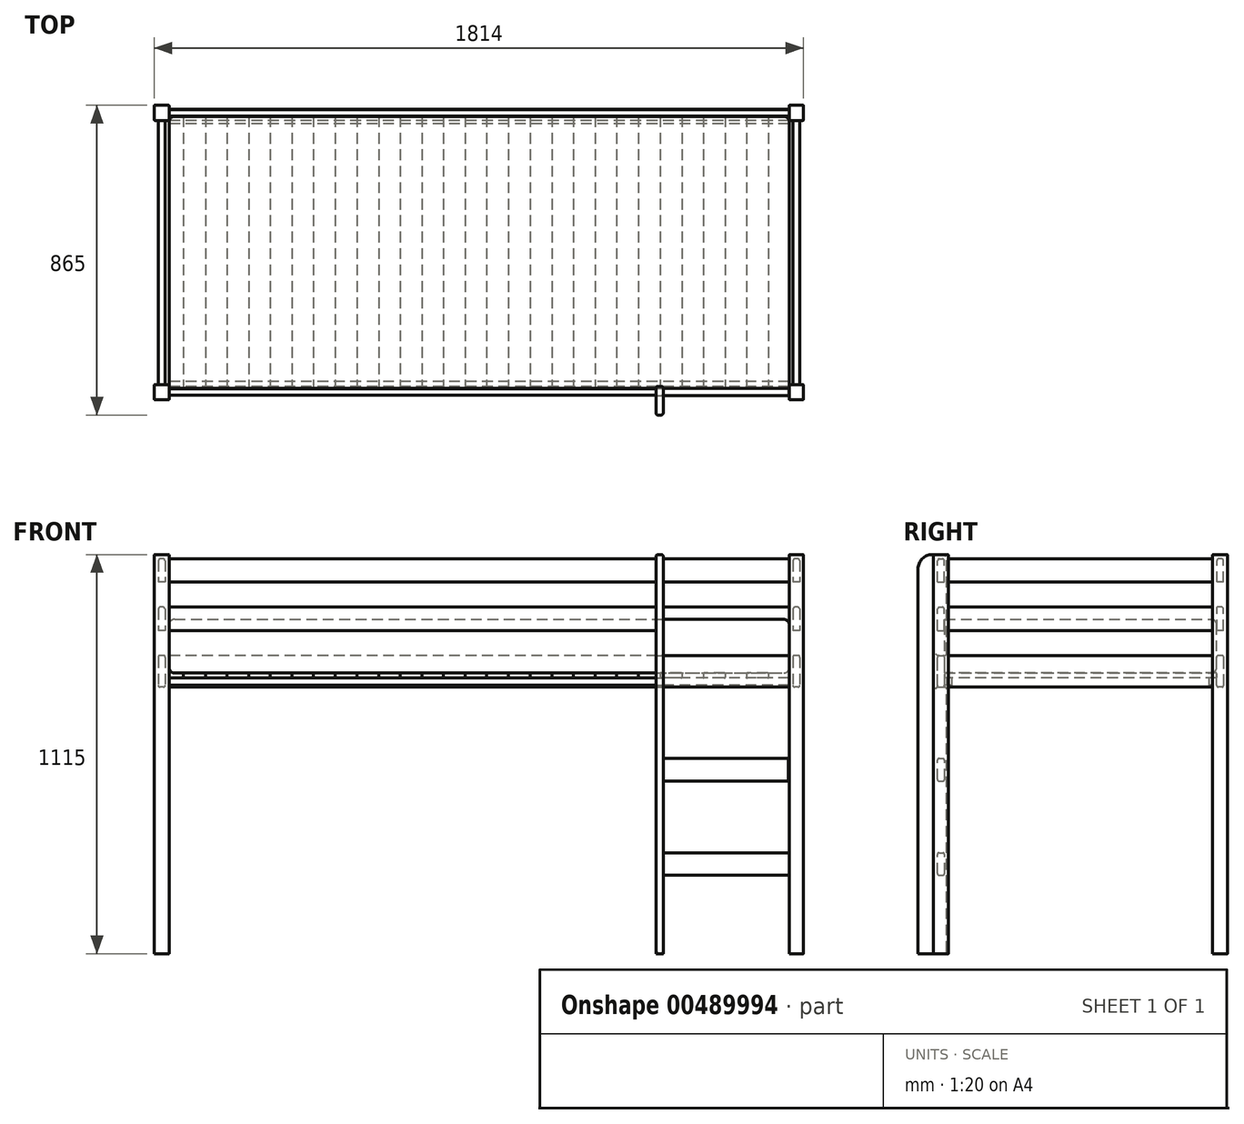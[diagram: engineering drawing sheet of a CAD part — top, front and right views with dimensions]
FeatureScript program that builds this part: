
annotation { "Feature Type Name" : "Feature", "Feature Type Description" : "" }
export const myFeature = defineFeature(function(context is Context, id is Id, definition is map)
    precondition{}
    {
        {
            var Q0;
            Q0=qCreatedBy(makeId("Front.planeOp"),FACE);
            var sketch = newSketch(context, id + "F0", { "sketchPlane" : qUnion([Q0])});
            skLineSegment(sketch, "E0.bottom", {"start": v(0, 0) * mm, "end": v(42, 0) * mm});
            skLineSegment(sketch, "E0.top", {"start": v(0, 1115) * mm, "end": v(42, 1115) * mm});
            skLineSegment(sketch, "E0.left", {"start": v(0, 0) * mm, "end": v(0, 1115) * mm});
            skLineSegment(sketch, "E0.right", {"start": v(42, 0) * mm, "end": v(42, 1115) * mm});
            skLineSegment(sketch, "E1.bottom", {"start": v(42, 745) * mm, "end": v(1774, 745) * mm});
            skLineSegment(sketch, "E1.top", {"start": v(42, 833) * mm, "end": v(1774, 833) * mm});
            skLineSegment(sketch, "E1.left", {"start": v(42, 745) * mm, "end": v(42, 833) * mm});
            skLineSegment(sketch, "E1.right", {"start": v(1774, 745) * mm, "end": v(1774, 833) * mm});
            skLineSegment(sketch, "E2.bottom", {"start": v(1774, 0) * mm, "end": v(1814, 0) * mm});
            skLineSegment(sketch, "E2.top", {"start": v(1774, 1115) * mm, "end": v(1814, 1115) * mm});
            skLineSegment(sketch, "E2.left", {"start": v(1774, 0) * mm, "end": v(1774, 1115) * mm});
            skLineSegment(sketch, "E2.right", {"start": v(1814, 0) * mm, "end": v(1814, 1115) * mm});
            skLineSegment(sketch, "E3.bottom", {"start": v(1402, 0) * mm, "end": v(1422, 0) * mm});
            skLineSegment(sketch, "E3.top", {"start": v(1402, 1115) * mm, "end": v(1422, 1115) * mm});
            skLineSegment(sketch, "E3.left", {"start": v(1402, 0) * mm, "end": v(1402, 1115) * mm});
            skLineSegment(sketch, "E3.right", {"start": v(1422, 0) * mm, "end": v(1422, 1115) * mm});
            skLineSegment(sketch, "E4.bottom", {"start": v(42, 968) * mm, "end": v(1402, 968) * mm});
            skLineSegment(sketch, "E4.top", {"start": v(42, 903) * mm, "end": v(1402, 903) * mm});
            skLineSegment(sketch, "E4.left", {"start": v(42, 968) * mm, "end": v(42, 903) * mm});
            skLineSegment(sketch, "E4.right", {"start": v(1402, 968) * mm, "end": v(1402, 903) * mm});
            skLineSegment(sketch, "E5.bottom", {"start": v(1422, 219) * mm, "end": v(1774, 219) * mm});
            skLineSegment(sketch, "E5.top", {"start": v(1422, 282) * mm, "end": v(1774, 282) * mm});
            skLineSegment(sketch, "E5.left", {"start": v(1422, 219) * mm, "end": v(1422, 282) * mm});
            skLineSegment(sketch, "E5.right", {"start": v(1774, 219) * mm, "end": v(1774, 282) * mm});
            skLineSegment(sketch, "E6.bottom", {"start": v(1422, 482) * mm, "end": v(1772, 482) * mm});
            skLineSegment(sketch, "E6.top", {"start": v(1422, 545) * mm, "end": v(1772, 545) * mm});
            skLineSegment(sketch, "E6.left", {"start": v(1422, 482) * mm, "end": v(1422, 545) * mm});
            skLineSegment(sketch, "E6.right", {"start": v(1772, 482) * mm, "end": v(1772, 545) * mm});
            skLineSegment(sketch, "E7.bottom", {"start": v(42, 1038) * mm, "end": v(1402, 1038) * mm});
            skLineSegment(sketch, "E7.top", {"start": v(42, 1103) * mm, "end": v(1402, 1103) * mm});
            skLineSegment(sketch, "E7.left", {"start": v(42, 1038) * mm, "end": v(42, 1103) * mm});
            skLineSegment(sketch, "E7.right", {"start": v(1402, 1038) * mm, "end": v(1402, 1103) * mm});
            skSolve(sketch);
        }
        {
            var Q0;
            {var subQ3=sQuery(id+"F0.wireOp",EDGE,"E2.bottom");Q0=makeQuery(id+"F0.imprint","IMPRINT",FACE,{"disambiguationData":[TD([[makeQuery(id+"F0.imprint","IMPRINT",EDGE,{"derivedFrom":subQ3}),1.0]])]});}
            var Q1;
            {var subQ1=sQuery(id+"F0.wireOp",EDGE,"E0.bottom");Q1=makeQuery(id+"F0.imprint","IMPRINT",FACE,{"disambiguationData":[TD([[makeQuery(id+"F0.imprint","IMPRINT",EDGE,{"derivedFrom":subQ1}),1.0]])]});}
            extrude(context, id + "F1", {"entities" : qUnion([Q0, Q1]), "depth" : 21 * mm, "hasSecondDirection" : true, "secondDirectionOppositeDirection" : true, "secondDirectionDepth" : 21 * mm});
        }
        {
            var Q0;
            {var subQ0=sQuery(id+"F0.wireOp",EDGE,"E1.left");Q0=makeQuery(id+"F0.imprint","IMPRINT",FACE,{"disambiguationData":[TD([[makeQuery(id+"F0.imprint","IMPRINT",EDGE,{"derivedFrom":subQ0}),-1.0]])]});}
            var Q1;
            {var subQ0=sQuery(id+"F0.wireOp",EDGE,"E2.left");var subQ1=sQuery(id+"F0.wireOp",EDGE,"E1.bottom");var subQ2=makeQuery(id+"F0.imprint","INTERSECT",VERTEX,{"derivedFrom":[subQ1,subQ0]});Q1=makeQuery(id+"F0.imprint","IMPRINT",FACE,{"disambiguationData":[TD([[makeQuery(id+"F0.imprint","IMPRINT",EDGE,{"disambiguationData":[TD([[subQ2,1.0]])],"derivedFrom":subQ1}),1.0]])]});}
            var Q2;
            {var subQ0=sQuery(id+"F0.wireOp",EDGE,"E3.left");var subQ1=sQuery(id+"F0.wireOp",EDGE,"E1.bottom");var subQ2=makeQuery(id+"F0.imprint","INTERSECT",VERTEX,{"derivedFrom":[subQ1,subQ0]});Q2=makeQuery(id+"F0.imprint","IMPRINT",FACE,{"disambiguationData":[TD([[makeQuery(id+"F0.imprint","IMPRINT",EDGE,{"disambiguationData":[TD([[subQ2,-1.0]])],"derivedFrom":subQ1}),1.0]])]});}
            var Q3;
            Q3=makeQuery(id+"F0.imprint","IMPRINT",FACE,{"disambiguationData":[TD([[makeQuery(id+"F0.imprint","IMPRINT",EDGE,{"derivedFrom":sQuery(id+"F0.wireOp",EDGE,"E6.bottom")}),1.0]])]});
            var Q4;
            Q4=makeQuery(id+"F0.imprint","IMPRINT",FACE,{"disambiguationData":[TD([[makeQuery(id+"F0.imprint","IMPRINT",EDGE,{"derivedFrom":sQuery(id+"F0.wireOp",EDGE,"E5.bottom")}),1.0]])]});
            extrude(context, id + "F2", {"entities" : qUnion([Q0, Q1, Q2, Q3, Q4]), "depth" : 10 * mm, "hasSecondDirection" : true, "secondDirectionOppositeDirection" : true, "secondDirectionDepth" : 10 * mm});
        }
        {
            var Q0;
            Q0=makeQuery(id+"F0.imprint","IMPRINT",FACE,{"disambiguationData":[TD([[makeQuery(id+"F0.imprint","IMPRINT",EDGE,{"derivedFrom":sQuery(id+"F0.wireOp",EDGE,"E7.bottom")}),1.0]])]});
            var Q1;
            Q1=makeQuery(id+"F0.imprint","IMPRINT",FACE,{"disambiguationData":[TD([[makeQuery(id+"F0.imprint","IMPRINT",EDGE,{"derivedFrom":sQuery(id+"F0.wireOp",EDGE,"E4.bottom")}),-1.0]])]});
            extrude(context, id + "F3", {"entities" : qUnion([Q0, Q1]), "operationType" : NewBodyOperationType.ADD, "depth" : 9 * mm, "hasSecondDirection" : true, "secondDirectionOppositeDirection" : true, "secondDirectionDepth" : 9 * mm});
        }
        {
            var Q0;
            {var subQ0=sQuery(id+"F0.wireOp",EDGE,"E3.bottom");Q0=makeQuery(id+"F0.imprint","IMPRINT",FACE,{"disambiguationData":[TD([[makeQuery(id+"F0.imprint","IMPRINT",EDGE,{"derivedFrom":subQ0}),1.0]])]});}
            var Q1;
            {var subQ0=sQuery(id+"F0.wireOp",EDGE,"E3.left");var subQ1=sQuery(id+"F0.wireOp",EDGE,"E1.bottom");var subQ2=makeQuery(id+"F0.imprint","INTERSECT",VERTEX,{"derivedFrom":[subQ1,subQ0]});Q1=makeQuery(id+"F0.imprint","IMPRINT",FACE,{"disambiguationData":[TD([[makeQuery(id+"F0.imprint","IMPRINT",EDGE,{"disambiguationData":[TD([[subQ2,-1.0]])],"derivedFrom":subQ1}),1.0]])]});}
            var Q2;
            {var subQ4=sQuery(id+"F0.wireOp",EDGE,"E3.top");Q2=makeQuery(id+"F0.imprint","IMPRINT",FACE,{"disambiguationData":[TD([[makeQuery(id+"F0.imprint","IMPRINT",EDGE,{"derivedFrom":subQ4}),-1.0]])]});}
            extrude(context, id + "F4", {"entities" : qUnion([Q0, Q1, Q2]), "depth" : 64 * mm, "hasSecondDirection" : true, "secondDirectionOppositeDirection" : true, "secondDirectionDepth" : 16 * mm});
        }
        {
            var Q0;
            Q0=makeQuery(id+"F4.opExtrude","CAP_EDGE",EDGE,{"disambiguationData":[OSD([sQuery(id+"F0.wireOp",EDGE,"E3.top")])],"isStart":false});
            fillet(context, id + "F5", {"entities" : qUnion([Q0]), "radius" : 40 * mm, "tangentPropagation" : true, "allowEdgeOverflow" : false});
        }
        {
            var Q0;
            Q0=makeQuery(id+"F2.opExtrude","SWEPT_BODY",BODY,{"disambiguationData":[OSD([sQuery(id+"F0.wireOp",EDGE,"E1.bottom"),sQuery(id+"F0.wireOp",EDGE,"E1.top"),sQuery(id+"F0.wireOp",EDGE,"E1.left"),sQuery(id+"F0.wireOp",EDGE,"E2.left")])]});
            var Q1;
            Q1=makeQuery(id+"F4.opExtrude","SWEPT_BODY",BODY,{"disambiguationData":[OSD([sQuery(id+"F0.wireOp",EDGE,"E3.bottom"),sQuery(id+"F0.wireOp",EDGE,"E3.top"),sQuery(id+"F0.wireOp",EDGE,"E3.left"),sQuery(id+"F0.wireOp",EDGE,"E3.right"),sQuery(id+"F0.wireOp",EDGE,"E4.right"),sQuery(id+"F0.wireOp",EDGE,"E5.left"),sQuery(id+"F0.wireOp",EDGE,"E6.left"),sQuery(id+"F0.wireOp",EDGE,"E7.right")])]});
            var Q2;
            Q2=makeQuery(id+"F2.opExtrude","CAP_FACE",FACE,{"disambiguationData":[OSD([sQuery(id+"F0.wireOp",EDGE,"E1.bottom"),sQuery(id+"F0.wireOp",EDGE,"E1.top"),sQuery(id+"F0.wireOp",EDGE,"E1.left"),sQuery(id+"F0.wireOp",EDGE,"E2.left")])],"isStart":true});
            booleanBodies(context, id + "F6", {"operationType" : BooleanOperationType.SUBTRACTION, "tools" : qUnion([Q0]), "targets" : qUnion([Q1]), "entitiesToOffset" : qUnion([Q2]), "keepTools" : true});
        }
        {
            var Q0;
            Q0=makeQuery(id+"F4.opExtrude","SWEPT_FACE",FACE,{"disambiguationData":[OSD([sQuery(id+"F0.wireOp",EDGE,"E3.right"),sQuery(id+"F0.wireOp",EDGE,"E5.left"),sQuery(id+"F0.wireOp",EDGE,"E6.left")])]});
            var sketch = newSketch(context, id + "F7", { "sketchPlane" : qUnion([Q0])});
            skLineSegment(sketch, "E8.bottom", {"start": v(10, 833) * mm, "end": v(10, 833) * mm});
            skLineSegment(sketch, "E8.top", {"start": v(10, 745) * mm, "end": v(10, 745) * mm});
            skLineSegment(sketch, "E8.left", {"start": v(10, 833) * mm, "end": v(10, 745) * mm});
            skLineSegment(sketch, "E8.right", {"start": v(16, 833) * mm, "end": v(16, 745) * mm});
            skLineSegment(sketch, "E9", {"start": v(16, 739) * mm, "end": v(16, 739) * mm});
            skPoint(sketch, "E10.visualSharp", {"position": v(16, 745) * mm});
            skArc(sketch, "E10.filletArc", {"start": v(16, 739) * mm, "mid": v(14.24, 743.24) * mm, "end": v(10, 745) * mm});
            skLineSegment(sketch, "E11", {"start": v(16, 839) * mm, "end": v(16, 839) * mm});
            skPoint(sketch, "E12.visualSharp", {"position": v(16, 833) * mm});
            skArc(sketch, "E12.filletArc", {"start": v(10, 833) * mm, "mid": v(14.24, 834.76) * mm, "end": v(16, 839) * mm});
            skLineSegment(sketch, "E13", {"start": v(10, 745) * mm, "end": v(10, 750) * mm, "construction": true});
            skLineSegment(sketch, "E14.bottom", {"start": v(10, 750) * mm, "end": v(30, 750) * mm});
            skLineSegment(sketch, "E14.top", {"start": v(10, 770) * mm, "end": v(30, 770) * mm});
            skLineSegment(sketch, "E14.left", {"start": v(10, 750) * mm, "end": v(10, 770) * mm});
            skLineSegment(sketch, "E14.right", {"start": v(30, 750) * mm, "end": v(30, 770) * mm});
            skSolve(sketch);
        }
        {
            var Q0;
            {var subQ10=sQuery(id+"F7.wireOp",EDGE,"E12.filletArc");Q0=makeQuery(id+"F7.imprint","IMPRINT",FACE,{"disambiguationData":[TD([[makeQuery(id+"F7.imprint","IMPRINT",EDGE,{"derivedFrom":subQ10}),-1.0]])]});}
            var Q1;
            {var subQ5=sQuery(id+"F7.wireOp",EDGE,"E14.left");Q1=makeQuery(id+"F7.imprint","IMPRINT",FACE,{"disambiguationData":[TD([[makeQuery(id+"F7.imprint","IMPRINT",EDGE,{"derivedFrom":subQ5}),-1.0]])]});}
            var Q2;
            {var subQ10=sQuery(id+"F7.wireOp",EDGE,"E10.filletArc");Q2=makeQuery(id+"F7.imprint","IMPRINT",FACE,{"disambiguationData":[TD([[makeQuery(id+"F7.imprint","IMPRINT",EDGE,{"derivedFrom":subQ10}),-1.0]])]});}
            extrude(context, id + "F8", {"entities" : qUnion([Q0, Q1, Q2]), "operationType" : NewBodyOperationType.REMOVE, "oppositeDirection" : true, "depth" : 25 * mm});
        }
        {
            var Q0;
            {var subQ5=sQuery(id+"F7.wireOp",EDGE,"E14.left");Q0=makeQuery(id+"F7.imprint","IMPRINT",FACE,{"disambiguationData":[TD([[makeQuery(id+"F7.imprint","IMPRINT",EDGE,{"derivedFrom":subQ5}),-1.0]])]});}
            var Q1;
            {var subQ5=sQuery(id+"F7.wireOp",EDGE,"E14.right");Q1=makeQuery(id+"F7.imprint","IMPRINT",FACE,{"disambiguationData":[TD([[makeQuery(id+"F7.imprint","IMPRINT",EDGE,{"derivedFrom":subQ5}),1.0]])]});}
            var Q2;
            Q2=makeQuery(id+"F1.opExtrude","SWEPT_FACE",FACE,{"disambiguationData":[OSD([sQuery(id+"F0.wireOp",EDGE,"E2.left"),sQuery(id+"F0.wireOp",EDGE,"E5.right")])]});
            var Q3;
            Q3=makeQuery(id+"F1.opExtrude","SWEPT_FACE",FACE,{"disambiguationData":[OSD([sQuery(id+"F0.wireOp",EDGE,"E0.right"),sQuery(id+"F0.wireOp",EDGE,"E1.left"),sQuery(id+"F0.wireOp",EDGE,"E4.left"),sQuery(id+"F0.wireOp",EDGE,"E7.left")])]});
            extrude(context, id + "F9", {"entities" : qUnion([Q0, Q1]), "endBound" : BoundingType.UP_TO_SURFACE, "endBoundEntityFace" : qUnion([Q2]), "depth" : 50 * mm, "hasSecondDirection" : true, "secondDirectionBound" : SecondDirectionBoundingType.UP_TO_SURFACE, "secondDirectionOppositeDirection" : true, "secondDirectionBoundEntityFace" : qUnion([Q3]), "secondDirectionDepth" : 25 * mm});
        }
        {
            var Q0;
            Q0=makeQuery(id+"F1.opExtrude","CAP_FACE",FACE,{"disambiguationData":[OSD([sQuery(id+"F0.wireOp",EDGE,"E2.bottom"),sQuery(id+"F0.wireOp",EDGE,"E2.top"),sQuery(id+"F0.wireOp",EDGE,"E2.left"),sQuery(id+"F0.wireOp",EDGE,"E2.right"),sQuery(id+"F0.wireOp",EDGE,"E5.right")])],"isStart":true});
            var sketch = newSketch(context, id + "F10", { "sketchPlane" : qUnion([Q0])});
            skLineSegment(sketch, "E15.bottom", {"start": v(-1804, 833) * mm, "end": v(-1784, 833) * mm});
            skLineSegment(sketch, "E15.top", {"start": v(-1804, 745) * mm, "end": v(-1784, 745) * mm});
            skLineSegment(sketch, "E15.left", {"start": v(-1804, 833) * mm, "end": v(-1804, 745) * mm});
            skLineSegment(sketch, "E15.right", {"start": v(-1784, 833) * mm, "end": v(-1784, 745) * mm});
            skLineSegment(sketch, "E16.bottom", {"start": v(-31, 833) * mm, "end": v(-11, 833) * mm});
            skLineSegment(sketch, "E16.top", {"start": v(-31, 745) * mm, "end": v(-11, 745) * mm});
            skLineSegment(sketch, "E16.left", {"start": v(-31, 833) * mm, "end": v(-31, 745) * mm});
            skLineSegment(sketch, "E16.right", {"start": v(-11, 833) * mm, "end": v(-11, 745) * mm});
            skLineSegment(sketch, "E17", {"start": v(-42, 833) * mm, "end": v(0, 833) * mm, "construction": true});
            skPoint(sketch, "E18", {"position": v(-21, 833) * mm});
            skLineSegment(sketch, "E19", {"start": v(-1814, 833) * mm, "end": v(-1774, 833) * mm, "construction": true});
            skPoint(sketch, "E20", {"position": v(-1794, 833) * mm});
            skLineSegment(sketch, "E21.bottom", {"start": v(-30, 1103) * mm, "end": v(-12, 1103) * mm});
            skLineSegment(sketch, "E21.top", {"start": v(-30, 1038) * mm, "end": v(-12, 1038) * mm});
            skLineSegment(sketch, "E21.left", {"start": v(-30, 1103) * mm, "end": v(-30, 1038) * mm});
            skLineSegment(sketch, "E21.right", {"start": v(-12, 1103) * mm, "end": v(-12, 1038) * mm});
            skLineSegment(sketch, "E22.bottom", {"start": v(-30, 968) * mm, "end": v(-12, 968) * mm});
            skLineSegment(sketch, "E22.top", {"start": v(-30, 903) * mm, "end": v(-12, 903) * mm});
            skLineSegment(sketch, "E22.left", {"start": v(-30, 968) * mm, "end": v(-30, 903) * mm});
            skLineSegment(sketch, "E22.right", {"start": v(-12, 968) * mm, "end": v(-12, 903) * mm});
            skLineSegment(sketch, "E23", {"start": v(-42, 968) * mm, "end": v(0, 968) * mm, "construction": true});
            skLineSegment(sketch, "E24", {"start": v(-42, 1103) * mm, "end": v(0, 1103) * mm, "construction": true});
            skPoint(sketch, "E25", {"position": v(-21, 1103) * mm});
            skPoint(sketch, "E26", {"position": v(-21, 968) * mm});
            skLineSegment(sketch, "E27.bottom", {"start": v(-1803, 1103) * mm, "end": v(-1785, 1103) * mm});
            skLineSegment(sketch, "E27.top", {"start": v(-1803, 1038) * mm, "end": v(-1785, 1038) * mm});
            skLineSegment(sketch, "E27.left", {"start": v(-1803, 1103) * mm, "end": v(-1803, 1038) * mm});
            skLineSegment(sketch, "E27.right", {"start": v(-1785, 1103) * mm, "end": v(-1785, 1038) * mm});
            skLineSegment(sketch, "E28.bottom", {"start": v(-1803, 968) * mm, "end": v(-1785, 968) * mm});
            skLineSegment(sketch, "E28.top", {"start": v(-1803, 903) * mm, "end": v(-1785, 903) * mm});
            skLineSegment(sketch, "E28.left", {"start": v(-1803, 968) * mm, "end": v(-1803, 903) * mm});
            skLineSegment(sketch, "E28.right", {"start": v(-1785, 968) * mm, "end": v(-1785, 903) * mm});
            skLineSegment(sketch, "E29", {"start": v(-1814, 1103) * mm, "end": v(-1774, 1103) * mm, "construction": true});
            skLineSegment(sketch, "E30", {"start": v(-1814, 968) * mm, "end": v(-1774, 968) * mm, "construction": true});
            skPoint(sketch, "E31", {"position": v(-1794, 1103) * mm});
            skPoint(sketch, "E32", {"position": v(-1794, 968) * mm});
            skSolve(sketch);
        }
        {
            var Q0;
            Q0=makeQuery(id+"F10.imprint","IMPRINT",FACE,{"disambiguationData":[TD([[makeQuery(id+"F10.imprint","IMPRINT",EDGE,{"derivedFrom":sQuery(id+"F10.wireOp",EDGE,"E27.bottom")}),-1.0]])]});
            var Q1;
            Q1=makeQuery(id+"F10.imprint","IMPRINT",FACE,{"disambiguationData":[TD([[makeQuery(id+"F10.imprint","IMPRINT",EDGE,{"derivedFrom":sQuery(id+"F10.wireOp",EDGE,"E28.bottom")}),-1.0]])]});
            var Q2;
            Q2=makeQuery(id+"F10.imprint","IMPRINT",FACE,{"disambiguationData":[TD([[makeQuery(id+"F10.imprint","IMPRINT",EDGE,{"derivedFrom":sQuery(id+"F10.wireOp",EDGE,"E21.bottom")}),-1.0]])]});
            var Q3;
            Q3=makeQuery(id+"F10.imprint","IMPRINT",FACE,{"disambiguationData":[TD([[makeQuery(id+"F10.imprint","IMPRINT",EDGE,{"derivedFrom":sQuery(id+"F10.wireOp",EDGE,"E22.bottom")}),-1.0]])]});
            var Q4;
            Q4=makeQuery(id+"F10.imprint","IMPRINT",FACE,{"disambiguationData":[TD([[makeQuery(id+"F10.imprint","IMPRINT",EDGE,{"derivedFrom":sQuery(id+"F10.wireOp",EDGE,"E16.bottom")}),-1.0]])]});
            var Q5;
            Q5=makeQuery(id+"F10.imprint","IMPRINT",FACE,{"disambiguationData":[TD([[makeQuery(id+"F10.imprint","IMPRINT",EDGE,{"derivedFrom":sQuery(id+"F10.wireOp",EDGE,"E15.bottom")}),-1.0]])]});
            extrude(context, id + "F11", {"entities" : qUnion([Q0, Q1, Q2, Q3, Q4, Q5]), "depth" : 738 * mm});
        }
        {
            var Q0;
            Q0=makeQuery(id+"F11.opExtrude","CAP_FACE",FACE,{"disambiguationData":[OSD([sQuery(id+"F10.wireOp",EDGE,"E27.bottom"),sQuery(id+"F10.wireOp",EDGE,"E27.top"),sQuery(id+"F10.wireOp",EDGE,"E27.left"),sQuery(id+"F10.wireOp",EDGE,"E27.right")])],"isStart":false});
            var sketch = newSketch(context, id + "F12", { "sketchPlane" : qUnion([Q0])});
            skLineSegment(sketch, "E33.bottom", {"start": v(-42, 1115) * mm, "end": v(0, 1115) * mm});
            skLineSegment(sketch, "E33.top", {"start": v(-42, 0) * mm, "end": v(0, 0) * mm});
            skLineSegment(sketch, "E33.left", {"start": v(-42, 1115) * mm, "end": v(-42, 0) * mm});
            skLineSegment(sketch, "E33.right", {"start": v(0, 1115) * mm, "end": v(0, 0) * mm});
            skLineSegment(sketch, "E34.bottom", {"start": v(-1814, 1115) * mm, "end": v(-1774, 1115) * mm});
            skLineSegment(sketch, "E34.top", {"start": v(-1814, 0) * mm, "end": v(-1774, 0) * mm});
            skLineSegment(sketch, "E34.left", {"start": v(-1814, 1115) * mm, "end": v(-1814, 0) * mm});
            skLineSegment(sketch, "E34.right", {"start": v(-1774, 1115) * mm, "end": v(-1774, 0) * mm});
            skSolve(sketch);
        }
        {
            var Q0;
            Q0=makeQuery(id+"F12.imprint","IMPRINT",FACE,{"disambiguationData":[TD([[makeQuery(id+"F12.imprint","IMPRINT",EDGE,{"derivedFrom":sQuery(id+"F12.wireOp",EDGE,"E34.bottom")}),-1.0]])]});
            var Q1;
            Q1=makeQuery(id+"F12.imprint","IMPRINT",FACE,{"disambiguationData":[TD([[makeQuery(id+"F12.imprint","IMPRINT",EDGE,{"derivedFrom":sQuery(id+"F12.wireOp",EDGE,"E33.bottom")}),-1.0]])]});
            var Q2;
            Q2=makeQuery(id+"F12.imprint","IMPRINT",FACE,{"disambiguationData":[TD([[makeQuery(id+"F12.imprint","IMPRINT",EDGE,{"derivedFrom":makeQuery(id+"F11.opExtrude","CAP_EDGE",EDGE,{"disambiguationData":[OSD([sQuery(id+"F10.wireOp",EDGE,"E27.bottom")])],"isStart":false})}),-1.0]])]});
            extrude(context, id + "F13", {"entities" : qUnion([Q0, Q1, Q2]), "depth" : 42 * mm});
        }
        {
            var Q0;
            Q0=makeQuery(id+"F13.opExtrude","SWEPT_FACE",FACE,{"disambiguationData":[OSD([sQuery(id+"F12.wireOp",EDGE,"E33.left")])]});
            var sketch = newSketch(context, id + "F14", { "sketchPlane" : qUnion([Q0])});
            skLineSegment(sketch, "E35.bottom", {"start": v(771, 1103) * mm, "end": v(789, 1103) * mm});
            skLineSegment(sketch, "E35.top", {"start": v(771, 1038) * mm, "end": v(789, 1038) * mm});
            skLineSegment(sketch, "E35.left", {"start": v(771, 1103) * mm, "end": v(771, 1038) * mm});
            skLineSegment(sketch, "E35.right", {"start": v(789, 1103) * mm, "end": v(789, 1038) * mm});
            skLineSegment(sketch, "E36.bottom", {"start": v(771, 968) * mm, "end": v(789, 968) * mm});
            skLineSegment(sketch, "E36.top", {"start": v(771, 903) * mm, "end": v(789, 903) * mm});
            skLineSegment(sketch, "E36.left", {"start": v(771, 968) * mm, "end": v(771, 903) * mm});
            skLineSegment(sketch, "E36.right", {"start": v(789, 968) * mm, "end": v(789, 903) * mm});
            skLineSegment(sketch, "E37.bottom", {"start": v(770, 833) * mm, "end": v(790, 833) * mm});
            skLineSegment(sketch, "E37.top", {"start": v(770, 745) * mm, "end": v(790, 745) * mm});
            skLineSegment(sketch, "E37.left", {"start": v(770, 833) * mm, "end": v(770, 745) * mm});
            skLineSegment(sketch, "E37.right", {"start": v(790, 833) * mm, "end": v(790, 745) * mm});
            skLineSegment(sketch, "E38.bottom", {"start": v(750, 770) * mm, "end": v(770, 770) * mm});
            skLineSegment(sketch, "E38.top", {"start": v(750, 750) * mm, "end": v(770, 750) * mm});
            skLineSegment(sketch, "E38.left", {"start": v(750, 770) * mm, "end": v(750, 750) * mm});
            skLineSegment(sketch, "E38.right", {"start": v(770, 770) * mm, "end": v(770, 750) * mm});
            skLineSegment(sketch, "E39", {"start": v(759, 1103) * mm, "end": v(801, 1103) * mm, "construction": true});
            skLineSegment(sketch, "E40", {"start": v(759, 968) * mm, "end": v(801, 968) * mm, "construction": true});
            skLineSegment(sketch, "E41", {"start": v(759, 833) * mm, "end": v(801, 833) * mm, "construction": true});
            skPoint(sketch, "E42", {"position": v(780, 1103) * mm});
            skPoint(sketch, "E43", {"position": v(780, 968) * mm});
            skPoint(sketch, "E44", {"position": v(780, 833) * mm});
            skLineSegment(sketch, "E45", {"start": v(770, 745) * mm, "end": v(770, 750) * mm, "construction": true});
            skSolve(sketch);
        }
        {
            var Q0;
            Q0=makeQuery(id+"F14.imprint","IMPRINT",FACE,{"disambiguationData":[TD([[makeQuery(id+"F14.imprint","IMPRINT",EDGE,{"derivedFrom":sQuery(id+"F14.wireOp",EDGE,"E35.bottom")}),-1.0]])]});
            var Q1;
            Q1=makeQuery(id+"F14.imprint","IMPRINT",FACE,{"disambiguationData":[TD([[makeQuery(id+"F14.imprint","IMPRINT",EDGE,{"derivedFrom":sQuery(id+"F14.wireOp",EDGE,"E36.bottom")}),-1.0]])]});
            var Q2;
            {var subQ3=sQuery(id+"F14.wireOp",EDGE,"E37.bottom");Q2=makeQuery(id+"F14.imprint","IMPRINT",FACE,{"disambiguationData":[TD([[makeQuery(id+"F14.imprint","IMPRINT",EDGE,{"derivedFrom":subQ3}),-1.0]])]});}
            var Q3;
            Q3=makeQuery(id+"F13.opExtrude","SWEPT_FACE",FACE,{"disambiguationData":[OSD([sQuery(id+"F12.wireOp",EDGE,"E34.right")])]});
            extrude(context, id + "F15", {"entities" : qUnion([Q0, Q1, Q2]), "endBound" : BoundingType.UP_TO_SURFACE, "endBoundEntityFace" : qUnion([Q3]), "depth" : 25 * mm});
        }
        {
            var Q0;
            {var subQ0=sQuery(id+"F14.wireOp",EDGE,"E38.right");Q0=makeQuery(id+"F14.imprint","IMPRINT",FACE,{"disambiguationData":[TD([[makeQuery(id+"F14.imprint","IMPRINT",EDGE,{"derivedFrom":subQ0}),-1.0]])]});}
            var Q1;
            {var subQ0=sQuery(id+"F14.wireOp",EDGE,"E38.left");Q1=makeQuery(id+"F14.imprint","IMPRINT",FACE,{"disambiguationData":[TD([[makeQuery(id+"F14.imprint","IMPRINT",EDGE,{"derivedFrom":subQ0}),1.0]])]});}
            var Q2;
            Q2=makeQuery(id+"F13.opExtrude","SWEPT_FACE",FACE,{"disambiguationData":[OSD([sQuery(id+"F12.wireOp",EDGE,"E34.right")])]});
            extrude(context, id + "F16", {"entities" : qUnion([Q0, Q1]), "endBound" : BoundingType.UP_TO_SURFACE, "endBoundEntityFace" : qUnion([Q2]), "depth" : 25 * mm});
        }
        {
            var Q0;
            Q0=makeQuery(id+"F2.opExtrude","CAP_FACE",FACE,{"disambiguationData":[OSD([sQuery(id+"F0.wireOp",EDGE,"E1.bottom"),sQuery(id+"F0.wireOp",EDGE,"E1.top"),sQuery(id+"F0.wireOp",EDGE,"E1.left"),sQuery(id+"F0.wireOp",EDGE,"E2.left")])],"isStart":true});
            var sketch = newSketch(context, id + "F17", { "sketchPlane" : qUnion([Q0])});
            skLineSegment(sketch, "E46", {"start": v(-42, 770) * mm, "end": v(-82, 770) * mm, "construction": true});
            skLineSegment(sketch, "E47.bottom", {"start": v(-143, 784) * mm, "end": v(-82, 784) * mm});
            skLineSegment(sketch, "E47.top", {"start": v(-143, 770) * mm, "end": v(-82, 770) * mm});
            skLineSegment(sketch, "E47.left", {"start": v(-143, 784) * mm, "end": v(-143, 770) * mm});
            skLineSegment(sketch, "E47.right", {"start": v(-82, 784) * mm, "end": v(-82, 770) * mm});
            skLineSegment(sketch, "E48.1.0.0", {"start": v(-264, 784) * mm, "end": v(-264, 770) * mm});
            skLineSegment(sketch, "E48.1.0.1", {"start": v(-264, 784) * mm, "end": v(-203, 784) * mm});
            skLineSegment(sketch, "E48.1.0.2", {"start": v(-203, 784) * mm, "end": v(-203, 770) * mm});
            skLineSegment(sketch, "E48.1.0.3", {"start": v(-264, 770) * mm, "end": v(-203, 770) * mm});
            skLineSegment(sketch, "E48.2.0.0", {"start": v(-385, 784) * mm, "end": v(-385, 770) * mm});
            skLineSegment(sketch, "E48.2.0.1", {"start": v(-385, 784) * mm, "end": v(-324, 784) * mm});
            skLineSegment(sketch, "E48.2.0.2", {"start": v(-324, 784) * mm, "end": v(-324, 770) * mm});
            skLineSegment(sketch, "E48.2.0.3", {"start": v(-385, 770) * mm, "end": v(-324, 770) * mm});
            skLineSegment(sketch, "E48.3.0.0", {"start": v(-506, 784) * mm, "end": v(-506, 770) * mm});
            skLineSegment(sketch, "E48.3.0.1", {"start": v(-506, 784) * mm, "end": v(-445, 784) * mm});
            skLineSegment(sketch, "E48.3.0.2", {"start": v(-445, 784) * mm, "end": v(-445, 770) * mm});
            skLineSegment(sketch, "E48.3.0.3", {"start": v(-506, 770) * mm, "end": v(-445, 770) * mm});
            skLineSegment(sketch, "E48.4.0.0", {"start": v(-627, 784) * mm, "end": v(-627, 770) * mm});
            skLineSegment(sketch, "E48.4.0.1", {"start": v(-627, 784) * mm, "end": v(-566, 784) * mm});
            skLineSegment(sketch, "E48.4.0.2", {"start": v(-566, 784) * mm, "end": v(-566, 770) * mm});
            skLineSegment(sketch, "E48.4.0.3", {"start": v(-627, 770) * mm, "end": v(-566, 770) * mm});
            skLineSegment(sketch, "E48.5.0.0", {"start": v(-748, 784) * mm, "end": v(-748, 770) * mm});
            skLineSegment(sketch, "E48.5.0.1", {"start": v(-748, 784) * mm, "end": v(-687, 784) * mm});
            skLineSegment(sketch, "E48.5.0.2", {"start": v(-687, 784) * mm, "end": v(-687, 770) * mm});
            skLineSegment(sketch, "E48.5.0.3", {"start": v(-748, 770) * mm, "end": v(-687, 770) * mm});
            skLineSegment(sketch, "E48.6.0.0", {"start": v(-869, 784) * mm, "end": v(-869, 770) * mm});
            skLineSegment(sketch, "E48.6.0.1", {"start": v(-869, 784) * mm, "end": v(-808, 784) * mm});
            skLineSegment(sketch, "E48.6.0.2", {"start": v(-808, 784) * mm, "end": v(-808, 770) * mm});
            skLineSegment(sketch, "E48.6.0.3", {"start": v(-869, 770) * mm, "end": v(-808, 770) * mm});
            skLineSegment(sketch, "E48.7.0.0", {"start": v(-990, 784) * mm, "end": v(-990, 770) * mm});
            skLineSegment(sketch, "E48.7.0.1", {"start": v(-990, 784) * mm, "end": v(-929, 784) * mm});
            skLineSegment(sketch, "E48.7.0.2", {"start": v(-929, 784) * mm, "end": v(-929, 770) * mm});
            skLineSegment(sketch, "E48.7.0.3", {"start": v(-990, 770) * mm, "end": v(-929, 770) * mm});
            skLineSegment(sketch, "E48.8.0.0", {"start": v(-1111, 784) * mm, "end": v(-1111, 770) * mm});
            skLineSegment(sketch, "E48.8.0.1", {"start": v(-1111, 784) * mm, "end": v(-1050, 784) * mm});
            skLineSegment(sketch, "E48.8.0.2", {"start": v(-1050, 784) * mm, "end": v(-1050, 770) * mm});
            skLineSegment(sketch, "E48.8.0.3", {"start": v(-1111, 770) * mm, "end": v(-1050, 770) * mm});
            skLineSegment(sketch, "E48.9.0.0", {"start": v(-1232, 784) * mm, "end": v(-1232, 770) * mm});
            skLineSegment(sketch, "E48.9.0.1", {"start": v(-1232, 784) * mm, "end": v(-1171, 784) * mm});
            skLineSegment(sketch, "E48.9.0.2", {"start": v(-1171, 784) * mm, "end": v(-1171, 770) * mm});
            skLineSegment(sketch, "E48.9.0.3", {"start": v(-1232, 770) * mm, "end": v(-1171, 770) * mm});
            skLineSegment(sketch, "E48.10.0.0", {"start": v(-1353, 784) * mm, "end": v(-1353, 770) * mm});
            skLineSegment(sketch, "E48.10.0.1", {"start": v(-1353, 784) * mm, "end": v(-1292, 784) * mm});
            skLineSegment(sketch, "E48.10.0.2", {"start": v(-1292, 784) * mm, "end": v(-1292, 770) * mm});
            skLineSegment(sketch, "E48.10.0.3", {"start": v(-1353, 770) * mm, "end": v(-1292, 770) * mm});
            skLineSegment(sketch, "E48.11.0.0", {"start": v(-1474, 784) * mm, "end": v(-1474, 770) * mm});
            skLineSegment(sketch, "E48.11.0.1", {"start": v(-1474, 784) * mm, "end": v(-1413, 784) * mm});
            skLineSegment(sketch, "E48.11.0.2", {"start": v(-1413, 784) * mm, "end": v(-1413, 770) * mm});
            skLineSegment(sketch, "E48.11.0.3", {"start": v(-1474, 770) * mm, "end": v(-1413, 770) * mm});
            skLineSegment(sketch, "E48.12.0.0", {"start": v(-1595, 784) * mm, "end": v(-1595, 770) * mm});
            skLineSegment(sketch, "E48.12.0.1", {"start": v(-1595, 784) * mm, "end": v(-1534, 784) * mm});
            skLineSegment(sketch, "E48.12.0.2", {"start": v(-1534, 784) * mm, "end": v(-1534, 770) * mm});
            skLineSegment(sketch, "E48.12.0.3", {"start": v(-1595, 770) * mm, "end": v(-1534, 770) * mm});
            skLineSegment(sketch, "E48.13.0.0", {"start": v(-1716, 784) * mm, "end": v(-1716, 770) * mm});
            skLineSegment(sketch, "E48.13.0.1", {"start": v(-1716, 784) * mm, "end": v(-1655, 784) * mm});
            skLineSegment(sketch, "E48.13.0.2", {"start": v(-1655, 784) * mm, "end": v(-1655, 770) * mm});
            skLineSegment(sketch, "E48.13.0.3", {"start": v(-1716, 770) * mm, "end": v(-1655, 770) * mm});
            skLineSegment(sketch, "E48.direction1", {"start": v(-143, 770) * mm, "end": v(-264, 770) * mm, "construction": true});
            skSolve(sketch);
        }
        {
            var Q0;
            Q0=makeQuery(id+"F17.imprint","IMPRINT",FACE,{"disambiguationData":[TD([[makeQuery(id+"F17.imprint","IMPRINT",EDGE,{"derivedFrom":sQuery(id+"F17.wireOp",EDGE,"E48.12.0.0")}),1.0]])]});
            var Q1;
            Q1=makeQuery(id+"F17.imprint","IMPRINT",FACE,{"disambiguationData":[TD([[makeQuery(id+"F17.imprint","IMPRINT",EDGE,{"derivedFrom":sQuery(id+"F17.wireOp",EDGE,"E48.11.0.0")}),1.0]])]});
            var Q2;
            Q2=makeQuery(id+"F17.imprint","IMPRINT",FACE,{"disambiguationData":[TD([[makeQuery(id+"F17.imprint","IMPRINT",EDGE,{"derivedFrom":sQuery(id+"F17.wireOp",EDGE,"E48.10.0.0")}),1.0]])]});
            var Q3;
            Q3=makeQuery(id+"F17.imprint","IMPRINT",FACE,{"disambiguationData":[TD([[makeQuery(id+"F17.imprint","IMPRINT",EDGE,{"derivedFrom":sQuery(id+"F17.wireOp",EDGE,"E48.9.0.0")}),1.0]])]});
            var Q4;
            Q4=makeQuery(id+"F17.imprint","IMPRINT",FACE,{"disambiguationData":[TD([[makeQuery(id+"F17.imprint","IMPRINT",EDGE,{"derivedFrom":sQuery(id+"F17.wireOp",EDGE,"E48.8.0.0")}),1.0]])]});
            var Q5;
            Q5=makeQuery(id+"F17.imprint","IMPRINT",FACE,{"disambiguationData":[TD([[makeQuery(id+"F17.imprint","IMPRINT",EDGE,{"derivedFrom":sQuery(id+"F17.wireOp",EDGE,"E48.7.0.0")}),1.0]])]});
            var Q6;
            Q6=makeQuery(id+"F17.imprint","IMPRINT",FACE,{"disambiguationData":[TD([[makeQuery(id+"F17.imprint","IMPRINT",EDGE,{"derivedFrom":sQuery(id+"F17.wireOp",EDGE,"E48.6.0.0")}),1.0]])]});
            var Q7;
            Q7=makeQuery(id+"F17.imprint","IMPRINT",FACE,{"disambiguationData":[TD([[makeQuery(id+"F17.imprint","IMPRINT",EDGE,{"derivedFrom":sQuery(id+"F17.wireOp",EDGE,"E48.5.0.0")}),1.0]])]});
            var Q8;
            Q8=makeQuery(id+"F17.imprint","IMPRINT",FACE,{"disambiguationData":[TD([[makeQuery(id+"F17.imprint","IMPRINT",EDGE,{"derivedFrom":sQuery(id+"F17.wireOp",EDGE,"E48.4.0.0")}),1.0]])]});
            var Q9;
            Q9=makeQuery(id+"F17.imprint","IMPRINT",FACE,{"disambiguationData":[TD([[makeQuery(id+"F17.imprint","IMPRINT",EDGE,{"derivedFrom":sQuery(id+"F17.wireOp",EDGE,"E48.3.0.0")}),1.0]])]});
            var Q10;
            Q10=makeQuery(id+"F17.imprint","IMPRINT",FACE,{"disambiguationData":[TD([[makeQuery(id+"F17.imprint","IMPRINT",EDGE,{"derivedFrom":sQuery(id+"F17.wireOp",EDGE,"E48.2.0.0")}),1.0]])]});
            var Q11;
            Q11=makeQuery(id+"F17.imprint","IMPRINT",FACE,{"disambiguationData":[TD([[makeQuery(id+"F17.imprint","IMPRINT",EDGE,{"derivedFrom":sQuery(id+"F17.wireOp",EDGE,"E48.1.0.0")}),1.0]])]});
            var Q12;
            Q12=makeQuery(id+"F17.imprint","IMPRINT",FACE,{"disambiguationData":[TD([[makeQuery(id+"F17.imprint","IMPRINT",EDGE,{"derivedFrom":sQuery(id+"F17.wireOp",EDGE,"E47.bottom")}),-1.0]])]});
            var Q13;
            Q13=makeQuery(id+"F17.imprint","IMPRINT",FACE,{"disambiguationData":[TD([[makeQuery(id+"F17.imprint","IMPRINT",EDGE,{"derivedFrom":sQuery(id+"F17.wireOp",EDGE,"E48.13.0.0")}),1.0]])]});
            var Q14;
            Q14=makeQuery(id+"F15.opExtrude","SWEPT_FACE",FACE,{"disambiguationData":[OSD([sQuery(id+"F14.wireOp",EDGE,"E37.left"),sQuery(id+"F14.wireOp",EDGE,"E38.right")])]});
            extrude(context, id + "F18", {"entities" : qUnion([Q0, Q1, Q2, Q3, Q4, Q5, Q6, Q7, Q8, Q9, Q10, Q11, Q12, Q13]), "endBound" : BoundingType.UP_TO_SURFACE, "endBoundEntityFace" : qUnion([Q14]), "depth" : 25 * mm});
        }
        {
            var Q0;
            Q0=makeQuery(id+"F1.opExtrude","CAP_EDGE",EDGE,{"disambiguationData":[OSD([sQuery(id+"F0.wireOp",EDGE,"E0.right"),sQuery(id+"F0.wireOp",EDGE,"E1.left"),sQuery(id+"F0.wireOp",EDGE,"E4.left"),sQuery(id+"F0.wireOp",EDGE,"E7.left")])],"isStart":false});
            var Q1;
            Q1=makeQuery(id+"F1.opExtrude","CAP_EDGE",EDGE,{"disambiguationData":[OSD([sQuery(id+"F0.wireOp",EDGE,"E0.right"),sQuery(id+"F0.wireOp",EDGE,"E1.left"),sQuery(id+"F0.wireOp",EDGE,"E4.left"),sQuery(id+"F0.wireOp",EDGE,"E7.left")])],"isStart":true});
            var Q2;
            Q2=makeQuery(id+"F1.opExtrude","CAP_EDGE",EDGE,{"disambiguationData":[OSD([sQuery(id+"F0.wireOp",EDGE,"E0.left")])],"isStart":false});
            var Q3;
            Q3=makeQuery(id+"F1.opExtrude","CAP_EDGE",EDGE,{"disambiguationData":[OSD([sQuery(id+"F0.wireOp",EDGE,"E0.left")])],"isStart":true});
            var Q4;
            Q4=makeQuery(id+"F13.opExtrude","CAP_EDGE",EDGE,{"disambiguationData":[OSD([sQuery(id+"F12.wireOp",EDGE,"E33.right")])],"isStart":true});
            var Q5;
            Q5=makeQuery(id+"F13.opExtrude","CAP_EDGE",EDGE,{"disambiguationData":[OSD([sQuery(id+"F12.wireOp",EDGE,"E33.left")])],"isStart":true});
            var Q6;
            Q6=makeQuery(id+"F13.opExtrude","CAP_EDGE",EDGE,{"disambiguationData":[OSD([sQuery(id+"F12.wireOp",EDGE,"E33.left")])],"isStart":false});
            var Q7;
            Q7=makeQuery(id+"F13.opExtrude","CAP_EDGE",EDGE,{"disambiguationData":[OSD([sQuery(id+"F12.wireOp",EDGE,"E33.right")])],"isStart":false});
            var Q8;
            Q8=makeQuery(id+"F1.opExtrude","CAP_EDGE",EDGE,{"disambiguationData":[OSD([sQuery(id+"F0.wireOp",EDGE,"E2.left"),sQuery(id+"F0.wireOp",EDGE,"E5.right")])],"isStart":true});
            var Q9;
            Q9=makeQuery(id+"F1.opExtrude","CAP_EDGE",EDGE,{"disambiguationData":[OSD([sQuery(id+"F0.wireOp",EDGE,"E2.left"),sQuery(id+"F0.wireOp",EDGE,"E5.right")])],"isStart":false});
            var Q10;
            Q10=makeQuery(id+"F1.opExtrude","CAP_EDGE",EDGE,{"disambiguationData":[OSD([sQuery(id+"F0.wireOp",EDGE,"E2.right")])],"isStart":false});
            var Q11;
            Q11=makeQuery(id+"F1.opExtrude","CAP_EDGE",EDGE,{"disambiguationData":[OSD([sQuery(id+"F0.wireOp",EDGE,"E2.right")])],"isStart":true});
            var Q12;
            Q12=makeQuery(id+"F13.opExtrude","CAP_EDGE",EDGE,{"disambiguationData":[OSD([sQuery(id+"F12.wireOp",EDGE,"E34.right")])],"isStart":true});
            var Q13;
            Q13=makeQuery(id+"F13.opExtrude","CAP_EDGE",EDGE,{"disambiguationData":[OSD([sQuery(id+"F12.wireOp",EDGE,"E34.left")])],"isStart":true});
            var Q14;
            Q14=makeQuery(id+"F13.opExtrude","CAP_EDGE",EDGE,{"disambiguationData":[OSD([sQuery(id+"F12.wireOp",EDGE,"E34.left")])],"isStart":false});
            var Q15;
            Q15=makeQuery(id+"F13.opExtrude","CAP_EDGE",EDGE,{"disambiguationData":[OSD([sQuery(id+"F12.wireOp",EDGE,"E34.right")])],"isStart":false});
            var Q16;
            Q16=makeQuery(id+"F13.opExtrude","CAP_EDGE",EDGE,{"disambiguationData":[OSD([sQuery(id+"F12.wireOp",EDGE,"E34.bottom")])],"isStart":true});
            var Q17;
            Q17=makeQuery(id+"F13.opExtrude","SWEPT_EDGE",EDGE,{"disambiguationData":[OSD([sQuery(id+"F12.wireOp",EDGE,"E34.bottom"),sQuery(id+"F12.wireOp",EDGE,"E34.right")])]});
            var Q18;
            Q18=makeQuery(id+"F13.opExtrude","CAP_EDGE",EDGE,{"disambiguationData":[OSD([sQuery(id+"F12.wireOp",EDGE,"E34.bottom")])],"isStart":false});
            var Q19;
            Q19=makeQuery(id+"F13.opExtrude","SWEPT_EDGE",EDGE,{"disambiguationData":[OSD([sQuery(id+"F12.wireOp",EDGE,"E34.bottom"),sQuery(id+"F12.wireOp",EDGE,"E34.left")])]});
            var Q20;
            Q20=makeQuery(id+"F1.opExtrude","SWEPT_EDGE",EDGE,{"disambiguationData":[OSD([sQuery(id+"F0.wireOp",EDGE,"E2.top"),sQuery(id+"F0.wireOp",EDGE,"E2.left")])]});
            var Q21;
            Q21=makeQuery(id+"F1.opExtrude","CAP_EDGE",EDGE,{"disambiguationData":[OSD([sQuery(id+"F0.wireOp",EDGE,"E2.top")])],"isStart":false});
            var Q22;
            Q22=makeQuery(id+"F1.opExtrude","SWEPT_EDGE",EDGE,{"disambiguationData":[OSD([sQuery(id+"F0.wireOp",EDGE,"E2.top"),sQuery(id+"F0.wireOp",EDGE,"E2.right")])]});
            var Q23;
            Q23=makeQuery(id+"F1.opExtrude","CAP_EDGE",EDGE,{"disambiguationData":[OSD([sQuery(id+"F0.wireOp",EDGE,"E2.top")])],"isStart":true});
            var Q24;
            Q24=makeQuery(id+"F13.opExtrude","CAP_EDGE",EDGE,{"disambiguationData":[OSD([sQuery(id+"F12.wireOp",EDGE,"E33.bottom")])],"isStart":false});
            var Q25;
            Q25=makeQuery(id+"F13.opExtrude","SWEPT_EDGE",EDGE,{"disambiguationData":[OSD([sQuery(id+"F12.wireOp",EDGE,"E33.bottom"),sQuery(id+"F12.wireOp",EDGE,"E33.left")])]});
            var Q26;
            Q26=makeQuery(id+"F13.opExtrude","SWEPT_EDGE",EDGE,{"disambiguationData":[OSD([sQuery(id+"F12.wireOp",EDGE,"E33.bottom"),sQuery(id+"F12.wireOp",EDGE,"E33.right")])]});
            var Q27;
            Q27=makeQuery(id+"F13.opExtrude","CAP_EDGE",EDGE,{"disambiguationData":[OSD([sQuery(id+"F12.wireOp",EDGE,"E33.bottom")])],"isStart":true});
            var Q28;
            Q28=makeQuery(id+"F1.opExtrude","SWEPT_EDGE",EDGE,{"disambiguationData":[OSD([sQuery(id+"F0.wireOp",EDGE,"E0.top"),sQuery(id+"F0.wireOp",EDGE,"E0.left")])]});
            var Q29;
            Q29=makeQuery(id+"F1.opExtrude","CAP_EDGE",EDGE,{"disambiguationData":[OSD([sQuery(id+"F0.wireOp",EDGE,"E0.top")])],"isStart":false});
            var Q30;
            Q30=makeQuery(id+"F1.opExtrude","SWEPT_EDGE",EDGE,{"disambiguationData":[OSD([sQuery(id+"F0.wireOp",EDGE,"E0.top"),sQuery(id+"F0.wireOp",EDGE,"E0.right")])]});
            var Q31;
            Q31=makeQuery(id+"F1.opExtrude","CAP_EDGE",EDGE,{"disambiguationData":[OSD([sQuery(id+"F0.wireOp",EDGE,"E0.top")])],"isStart":true});
            fillet(context, id + "F19", {"entities" : qUnion([Q0, Q1, Q2, Q3, Q4, Q5, Q6, Q7, Q8, Q9, Q10, Q11, Q12, Q13, Q14, Q15, Q16, Q17, Q18, Q19, Q20, Q21, Q22, Q23, Q24, Q25, Q26, Q27, Q28, Q29, Q30, Q31]), "radius" : 1 * mm, "tangentPropagation" : true, "allowEdgeOverflow" : false});
        }
        {
            var Q0;
            Q0=makeQuery(id+"F4.opExtrude","CAP_EDGE",EDGE,{"disambiguationData":[OSD([sQuery(id+"F0.wireOp",EDGE,"E3.right"),sQuery(id+"F0.wireOp",EDGE,"E5.left"),sQuery(id+"F0.wireOp",EDGE,"E6.left")])],"isStart":false});
            var Q1;
            Q1=makeQuery(id+"F4.opExtrude","CAP_EDGE",EDGE,{"disambiguationData":[OSD([sQuery(id+"F0.wireOp",EDGE,"E3.left"),sQuery(id+"F0.wireOp",EDGE,"E4.right"),sQuery(id+"F0.wireOp",EDGE,"E7.right")])],"isStart":false});
            var Q2;
            Q2=makeQuery(id+"F3.opExtrude","CAP_EDGE",EDGE,{"disambiguationData":[OSD([sQuery(id+"F0.wireOp",EDGE,"E7.top")])],"isStart":true});
            var Q3;
            Q3=makeQuery(id+"F3.opExtrude","CAP_EDGE",EDGE,{"disambiguationData":[OSD([sQuery(id+"F0.wireOp",EDGE,"E7.top")])],"isStart":false});
            var Q4;
            Q4=makeQuery(id+"F3.opExtrude","CAP_EDGE",EDGE,{"disambiguationData":[OSD([sQuery(id+"F0.wireOp",EDGE,"E4.bottom")])],"isStart":true});
            var Q5;
            Q5=makeQuery(id+"F3.opExtrude","CAP_EDGE",EDGE,{"disambiguationData":[OSD([sQuery(id+"F0.wireOp",EDGE,"E4.bottom")])],"isStart":false});
            var Q6;
            Q6=makeQuery(id+"F2.opExtrude","CAP_EDGE",EDGE,{"disambiguationData":[OSD([sQuery(id+"F0.wireOp",EDGE,"E1.top")])],"isStart":true});
            var Q7;
            Q7=makeQuery(id+"F2.opExtrude","CAP_EDGE",EDGE,{"disambiguationData":[OSD([sQuery(id+"F0.wireOp",EDGE,"E1.top")])],"isStart":false});
            var Q8;
            Q8=makeQuery(id+"F15.opExtrude","SWEPT_EDGE",EDGE,{"disambiguationData":[OSD([sQuery(id+"F14.wireOp",EDGE,"E35.bottom"),sQuery(id+"F14.wireOp",EDGE,"E35.right")])]});
            var Q9;
            Q9=makeQuery(id+"F15.opExtrude","SWEPT_EDGE",EDGE,{"disambiguationData":[OSD([sQuery(id+"F14.wireOp",EDGE,"E35.bottom"),sQuery(id+"F14.wireOp",EDGE,"E35.left")])]});
            var Q10;
            Q10=makeQuery(id+"F15.opExtrude","SWEPT_EDGE",EDGE,{"disambiguationData":[OSD([sQuery(id+"F14.wireOp",EDGE,"E36.bottom"),sQuery(id+"F14.wireOp",EDGE,"E36.right")])]});
            var Q11;
            Q11=makeQuery(id+"F15.opExtrude","SWEPT_EDGE",EDGE,{"disambiguationData":[OSD([sQuery(id+"F14.wireOp",EDGE,"E37.bottom"),sQuery(id+"F14.wireOp",EDGE,"E37.right")])]});
            var Q12;
            Q12=makeQuery(id+"F15.opExtrude","SWEPT_EDGE",EDGE,{"disambiguationData":[OSD([sQuery(id+"F14.wireOp",EDGE,"E37.bottom"),sQuery(id+"F14.wireOp",EDGE,"E37.left")])]});
            var Q13;
            Q13=makeQuery(id+"F11.opExtrude","SWEPT_EDGE",EDGE,{"disambiguationData":[OSD([sQuery(id+"F10.wireOp",EDGE,"E27.bottom"),sQuery(id+"F10.wireOp",EDGE,"E27.right")])]});
            var Q14;
            Q14=makeQuery(id+"F11.opExtrude","SWEPT_EDGE",EDGE,{"disambiguationData":[OSD([sQuery(id+"F10.wireOp",EDGE,"E27.bottom"),sQuery(id+"F10.wireOp",EDGE,"E27.left")])]});
            var Q15;
            Q15=makeQuery(id+"F11.opExtrude","SWEPT_EDGE",EDGE,{"disambiguationData":[OSD([sQuery(id+"F10.wireOp",EDGE,"E28.bottom"),sQuery(id+"F10.wireOp",EDGE,"E28.right")])]});
            var Q16;
            Q16=makeQuery(id+"F11.opExtrude","SWEPT_EDGE",EDGE,{"disambiguationData":[OSD([sQuery(id+"F10.wireOp",EDGE,"E28.bottom"),sQuery(id+"F10.wireOp",EDGE,"E28.left")])]});
            var Q17;
            Q17=makeQuery(id+"F11.opExtrude","SWEPT_EDGE",EDGE,{"disambiguationData":[OSD([sQuery(id+"F10.wireOp",EDGE,"E15.bottom"),sQuery(id+"F10.wireOp",EDGE,"E15.right")])]});
            var Q18;
            Q18=makeQuery(id+"F11.opExtrude","SWEPT_EDGE",EDGE,{"disambiguationData":[OSD([sQuery(id+"F10.wireOp",EDGE,"E15.bottom"),sQuery(id+"F10.wireOp",EDGE,"E15.left")])]});
            var Q19;
            Q19=makeQuery(id+"F11.opExtrude","SWEPT_EDGE",EDGE,{"disambiguationData":[OSD([sQuery(id+"F10.wireOp",EDGE,"E21.bottom"),sQuery(id+"F10.wireOp",EDGE,"E21.right")])]});
            var Q20;
            Q20=makeQuery(id+"F11.opExtrude","SWEPT_EDGE",EDGE,{"disambiguationData":[OSD([sQuery(id+"F10.wireOp",EDGE,"E21.bottom"),sQuery(id+"F10.wireOp",EDGE,"E21.left")])]});
            var Q21;
            Q21=makeQuery(id+"F11.opExtrude","SWEPT_EDGE",EDGE,{"disambiguationData":[OSD([sQuery(id+"F10.wireOp",EDGE,"E22.bottom"),sQuery(id+"F10.wireOp",EDGE,"E22.right")])]});
            var Q22;
            Q22=makeQuery(id+"F11.opExtrude","SWEPT_EDGE",EDGE,{"disambiguationData":[OSD([sQuery(id+"F10.wireOp",EDGE,"E22.bottom"),sQuery(id+"F10.wireOp",EDGE,"E22.left")])]});
            var Q23;
            Q23=makeQuery(id+"F11.opExtrude","SWEPT_EDGE",EDGE,{"disambiguationData":[OSD([sQuery(id+"F10.wireOp",EDGE,"E16.bottom"),sQuery(id+"F10.wireOp",EDGE,"E16.right")])]});
            var Q24;
            Q24=makeQuery(id+"F11.opExtrude","SWEPT_EDGE",EDGE,{"disambiguationData":[OSD([sQuery(id+"F10.wireOp",EDGE,"E16.bottom"),sQuery(id+"F10.wireOp",EDGE,"E16.left")])]});
            var Q25;
            Q25=makeQuery(id+"F11.opExtrude","SWEPT_EDGE",EDGE,{"disambiguationData":[OSD([sQuery(id+"F10.wireOp",EDGE,"E16.top"),sQuery(id+"F10.wireOp",EDGE,"E16.right")])]});
            var Q26;
            Q26=makeQuery(id+"F11.opExtrude","SWEPT_EDGE",EDGE,{"disambiguationData":[OSD([sQuery(id+"F10.wireOp",EDGE,"E16.top"),sQuery(id+"F10.wireOp",EDGE,"E16.left")])]});
            var Q27;
            Q27=makeQuery(id+"F2.opExtrude","CAP_EDGE",EDGE,{"disambiguationData":[OSD([sQuery(id+"F0.wireOp",EDGE,"E1.bottom")])],"isStart":true});
            var Q28;
            Q28=makeQuery(id+"F2.opExtrude","CAP_EDGE",EDGE,{"disambiguationData":[OSD([sQuery(id+"F0.wireOp",EDGE,"E1.bottom")])],"isStart":false});
            var Q29;
            Q29=makeQuery(id+"F15.opExtrude","SWEPT_EDGE",EDGE,{"disambiguationData":[OSD([sQuery(id+"F14.wireOp",EDGE,"E37.top"),sQuery(id+"F14.wireOp",EDGE,"E37.left")])]});
            var Q30;
            Q30=makeQuery(id+"F15.opExtrude","SWEPT_EDGE",EDGE,{"disambiguationData":[OSD([sQuery(id+"F14.wireOp",EDGE,"E37.top"),sQuery(id+"F14.wireOp",EDGE,"E37.right")])]});
            var Q31;
            Q31=makeQuery(id+"F11.opExtrude","SWEPT_EDGE",EDGE,{"disambiguationData":[OSD([sQuery(id+"F10.wireOp",EDGE,"E15.top"),sQuery(id+"F10.wireOp",EDGE,"E15.right")])]});
            var Q32;
            Q32=makeQuery(id+"F11.opExtrude","SWEPT_EDGE",EDGE,{"disambiguationData":[OSD([sQuery(id+"F10.wireOp",EDGE,"E15.top"),sQuery(id+"F10.wireOp",EDGE,"E15.left")])]});
            var Q33;
            Q33=makeQuery(id+"F2.opExtrude","CAP_EDGE",EDGE,{"disambiguationData":[OSD([sQuery(id+"F0.wireOp",EDGE,"E5.bottom")])],"isStart":false});
            var Q34;
            Q34=makeQuery(id+"F2.opExtrude","CAP_EDGE",EDGE,{"disambiguationData":[OSD([sQuery(id+"F0.wireOp",EDGE,"E5.bottom")])],"isStart":true});
            var Q35;
            Q35=makeQuery(id+"F2.opExtrude","CAP_EDGE",EDGE,{"disambiguationData":[OSD([sQuery(id+"F0.wireOp",EDGE,"E6.bottom")])],"isStart":false});
            var Q36;
            Q36=makeQuery(id+"F2.opExtrude","CAP_EDGE",EDGE,{"disambiguationData":[OSD([sQuery(id+"F0.wireOp",EDGE,"E6.bottom")])],"isStart":true});
            var Q37;
            Q37=makeQuery(id+"F2.opExtrude","CAP_EDGE",EDGE,{"disambiguationData":[OSD([sQuery(id+"F0.wireOp",EDGE,"E6.top")])],"isStart":true});
            var Q38;
            Q38=makeQuery(id+"F2.opExtrude","CAP_EDGE",EDGE,{"disambiguationData":[OSD([sQuery(id+"F0.wireOp",EDGE,"E6.top")])],"isStart":false});
            var Q39;
            Q39=makeQuery(id+"F2.opExtrude","CAP_EDGE",EDGE,{"disambiguationData":[OSD([sQuery(id+"F0.wireOp",EDGE,"E5.top")])],"isStart":true});
            var Q40;
            Q40=makeQuery(id+"F2.opExtrude","CAP_EDGE",EDGE,{"disambiguationData":[OSD([sQuery(id+"F0.wireOp",EDGE,"E5.top")])],"isStart":false});
            var Q41;
            {var subQ0=sQuery(id+"F0.wireOp",EDGE,"E6.left");var subQ1=sQuery(id+"F0.wireOp",EDGE,"E5.left");var subQ2=sQuery(id+"F0.wireOp",EDGE,"E3.right");var subQ3=sQuery(id+"F0.wireOp",EDGE,"E3.top");Q41=makeQuery(id+"F8.boolean.opBoolean","SPLIT",EDGE,{"disambiguationData":[TD([makeQuery(id+"F4.opExtrude","SWEPT_FACE",FACE,{"disambiguationData":[OSD([subQ3])]})])],"derivedFrom":makeQuery(id+"F4.opExtrude","CAP_EDGE",EDGE,{"disambiguationData":[OSD([subQ2,subQ1,subQ0])],"isStart":true})});}
            var Q42;
            {var subQ0=sQuery(id+"F0.wireOp",EDGE,"E7.right");var subQ1=sQuery(id+"F0.wireOp",EDGE,"E4.right");var subQ2=sQuery(id+"F0.wireOp",EDGE,"E3.left");var subQ3=sQuery(id+"F0.wireOp",EDGE,"E3.top");Q42=makeQuery(id+"F8.boolean.opBoolean","SPLIT",EDGE,{"disambiguationData":[TD([makeQuery(id+"F4.opExtrude","SWEPT_FACE",FACE,{"disambiguationData":[OSD([subQ3])]})])],"derivedFrom":makeQuery(id+"F4.opExtrude","CAP_EDGE",EDGE,{"disambiguationData":[OSD([subQ2,subQ1,subQ0])],"isStart":true})});}
            var Q43;
            {var subQ0=sQuery(id+"F0.wireOp",EDGE,"E3.bottom");var subQ1=sQuery(id+"F0.wireOp",EDGE,"E7.right");var subQ2=sQuery(id+"F0.wireOp",EDGE,"E4.right");var subQ3=sQuery(id+"F0.wireOp",EDGE,"E3.left");Q43=makeQuery(id+"F8.boolean.opBoolean","SPLIT",EDGE,{"disambiguationData":[TD([makeQuery(id+"F4.opExtrude","SWEPT_FACE",FACE,{"disambiguationData":[OSD([subQ0])]})])],"derivedFrom":makeQuery(id+"F4.opExtrude","CAP_EDGE",EDGE,{"disambiguationData":[OSD([subQ3,subQ2,subQ1])],"isStart":true})});}
            var Q44;
            {var subQ0=sQuery(id+"F0.wireOp",EDGE,"E3.bottom");var subQ1=sQuery(id+"F0.wireOp",EDGE,"E6.left");var subQ2=sQuery(id+"F0.wireOp",EDGE,"E5.left");var subQ3=sQuery(id+"F0.wireOp",EDGE,"E3.right");var subQ4=sQuery(id+"F0.wireOp",EDGE,"E7.right");var subQ5=sQuery(id+"F0.wireOp",EDGE,"E4.right");var subQ6=sQuery(id+"F0.wireOp",EDGE,"E3.left");Q44=makeQuery(id+"F8.boolean.opBoolean","SPLIT",FACE,{"disambiguationData":[TD([makeQuery(id+"F4.opExtrude","SWEPT_FACE",FACE,{"disambiguationData":[OSD([subQ0])]})])],"derivedFrom":makeQuery(id+"F4.opExtrude","CAP_FACE",FACE,{"disambiguationData":[OSD([subQ0,sQuery(id+"F0.wireOp",EDGE,"E3.top"),subQ6,subQ3,subQ5,subQ2,subQ1,subQ4])],"isStart":true})});}
            var Q45;
            Q45=makeQuery(id+"F6.opBoolean","INTERSECT",EDGE,{"derivedFrom":[makeQuery(id+"F2.opExtrude","CAP_FACE",FACE,{"disambiguationData":[OSD([sQuery(id+"F0.wireOp",EDGE,"E1.bottom"),sQuery(id+"F0.wireOp",EDGE,"E1.top"),sQuery(id+"F0.wireOp",EDGE,"E1.left"),sQuery(id+"F0.wireOp",EDGE,"E2.left")])],"isStart":false}),makeQuery(id+"F4.opExtrude","SWEPT_FACE",FACE,{"disambiguationData":[OSD([sQuery(id+"F0.wireOp",EDGE,"E3.right"),sQuery(id+"F0.wireOp",EDGE,"E5.left"),sQuery(id+"F0.wireOp",EDGE,"E6.left")])]})]});
            var Q46;
            Q46=makeQuery(id+"F6.opBoolean","INTERSECT",EDGE,{"derivedFrom":[makeQuery(id+"F2.opExtrude","CAP_FACE",FACE,{"disambiguationData":[OSD([sQuery(id+"F0.wireOp",EDGE,"E1.bottom"),sQuery(id+"F0.wireOp",EDGE,"E1.top"),sQuery(id+"F0.wireOp",EDGE,"E1.left"),sQuery(id+"F0.wireOp",EDGE,"E2.left")])],"isStart":false}),makeQuery(id+"F4.opExtrude","SWEPT_FACE",FACE,{"disambiguationData":[OSD([sQuery(id+"F0.wireOp",EDGE,"E3.left"),sQuery(id+"F0.wireOp",EDGE,"E4.right"),sQuery(id+"F0.wireOp",EDGE,"E7.right")])]})]});
            fillet(context, id + "F20", {"entities" : qUnion([Q0, Q1, Q2, Q3, Q4, Q5, Q6, Q7, Q8, Q9, Q10, Q11, Q12, Q13, Q14, Q15, Q16, Q17, Q18, Q19, Q20, Q21, Q22, Q23, Q24, Q25, Q26, Q27, Q28, Q29, Q30, Q31, Q32, Q33, Q34, Q35, Q36, Q37, Q38, Q39, Q40, Q41, Q42, Q43, Q44, Q45, Q46]), "radius" : 5 * mm, "tangentPropagation" : true, "allowEdgeOverflow" : false});
        }
        {
            var Q0;
            Q0=makeQuery(id+"F18.opExtrude","SWEPT_EDGE",EDGE,{"disambiguationData":[OSD([sQuery(id+"F17.wireOp",EDGE,"E48.13.0.1"),sQuery(id+"F17.wireOp",EDGE,"E48.13.0.2")])]});
            var Q1;
            Q1=makeQuery(id+"F18.opExtrude","SWEPT_EDGE",EDGE,{"disambiguationData":[OSD([sQuery(id+"F17.wireOp",EDGE,"E48.13.0.0"),sQuery(id+"F17.wireOp",EDGE,"E48.13.0.1")])]});
            var Q2;
            Q2=makeQuery(id+"F18.opExtrude","SWEPT_EDGE",EDGE,{"disambiguationData":[OSD([sQuery(id+"F17.wireOp",EDGE,"E48.12.0.0"),sQuery(id+"F17.wireOp",EDGE,"E48.12.0.1")])]});
            var Q3;
            Q3=makeQuery(id+"F18.opExtrude","SWEPT_EDGE",EDGE,{"disambiguationData":[OSD([sQuery(id+"F17.wireOp",EDGE,"E48.12.0.1"),sQuery(id+"F17.wireOp",EDGE,"E48.12.0.2")])]});
            var Q4;
            Q4=makeQuery(id+"F18.opExtrude","SWEPT_EDGE",EDGE,{"disambiguationData":[OSD([sQuery(id+"F17.wireOp",EDGE,"E47.bottom"),sQuery(id+"F17.wireOp",EDGE,"E47.right")])]});
            var Q5;
            Q5=makeQuery(id+"F18.opExtrude","SWEPT_EDGE",EDGE,{"disambiguationData":[OSD([sQuery(id+"F17.wireOp",EDGE,"E47.bottom"),sQuery(id+"F17.wireOp",EDGE,"E47.left")])]});
            var Q6;
            Q6=makeQuery(id+"F18.opExtrude","SWEPT_EDGE",EDGE,{"disambiguationData":[OSD([sQuery(id+"F17.wireOp",EDGE,"E48.1.0.1"),sQuery(id+"F17.wireOp",EDGE,"E48.1.0.2")])]});
            var Q7;
            Q7=makeQuery(id+"F18.opExtrude","SWEPT_EDGE",EDGE,{"disambiguationData":[OSD([sQuery(id+"F17.wireOp",EDGE,"E48.1.0.0"),sQuery(id+"F17.wireOp",EDGE,"E48.1.0.1")])]});
            var Q8;
            Q8=makeQuery(id+"F18.opExtrude","SWEPT_EDGE",EDGE,{"disambiguationData":[OSD([sQuery(id+"F17.wireOp",EDGE,"E48.2.0.1"),sQuery(id+"F17.wireOp",EDGE,"E48.2.0.2")])]});
            var Q9;
            Q9=makeQuery(id+"F18.opExtrude","SWEPT_EDGE",EDGE,{"disambiguationData":[OSD([sQuery(id+"F17.wireOp",EDGE,"E48.2.0.0"),sQuery(id+"F17.wireOp",EDGE,"E48.2.0.1")])]});
            var Q10;
            Q10=makeQuery(id+"F18.opExtrude","SWEPT_EDGE",EDGE,{"disambiguationData":[OSD([sQuery(id+"F17.wireOp",EDGE,"E48.3.0.1"),sQuery(id+"F17.wireOp",EDGE,"E48.3.0.2")])]});
            var Q11;
            Q11=makeQuery(id+"F18.opExtrude","SWEPT_EDGE",EDGE,{"disambiguationData":[OSD([sQuery(id+"F17.wireOp",EDGE,"E48.3.0.0"),sQuery(id+"F17.wireOp",EDGE,"E48.3.0.1")])]});
            var Q12;
            Q12=makeQuery(id+"F18.opExtrude","SWEPT_EDGE",EDGE,{"disambiguationData":[OSD([sQuery(id+"F17.wireOp",EDGE,"E48.4.0.0"),sQuery(id+"F17.wireOp",EDGE,"E48.4.0.1")])]});
            var Q13;
            Q13=makeQuery(id+"F18.opExtrude","SWEPT_EDGE",EDGE,{"disambiguationData":[OSD([sQuery(id+"F17.wireOp",EDGE,"E48.4.0.1"),sQuery(id+"F17.wireOp",EDGE,"E48.4.0.2")])]});
            var Q14;
            Q14=makeQuery(id+"F18.opExtrude","SWEPT_EDGE",EDGE,{"disambiguationData":[OSD([sQuery(id+"F17.wireOp",EDGE,"E48.5.0.1"),sQuery(id+"F17.wireOp",EDGE,"E48.5.0.2")])]});
            var Q15;
            Q15=makeQuery(id+"F18.opExtrude","SWEPT_EDGE",EDGE,{"disambiguationData":[OSD([sQuery(id+"F17.wireOp",EDGE,"E48.5.0.0"),sQuery(id+"F17.wireOp",EDGE,"E48.5.0.1")])]});
            var Q16;
            Q16=makeQuery(id+"F18.opExtrude","SWEPT_EDGE",EDGE,{"disambiguationData":[OSD([sQuery(id+"F17.wireOp",EDGE,"E48.6.0.0"),sQuery(id+"F17.wireOp",EDGE,"E48.6.0.1")])]});
            var Q17;
            Q17=makeQuery(id+"F18.opExtrude","SWEPT_EDGE",EDGE,{"disambiguationData":[OSD([sQuery(id+"F17.wireOp",EDGE,"E48.6.0.1"),sQuery(id+"F17.wireOp",EDGE,"E48.6.0.2")])]});
            var Q18;
            Q18=makeQuery(id+"F18.opExtrude","SWEPT_EDGE",EDGE,{"disambiguationData":[OSD([sQuery(id+"F17.wireOp",EDGE,"E48.7.0.0"),sQuery(id+"F17.wireOp",EDGE,"E48.7.0.1")])]});
            var Q19;
            Q19=makeQuery(id+"F18.opExtrude","SWEPT_EDGE",EDGE,{"disambiguationData":[OSD([sQuery(id+"F17.wireOp",EDGE,"E48.7.0.1"),sQuery(id+"F17.wireOp",EDGE,"E48.7.0.2")])]});
            var Q20;
            Q20=makeQuery(id+"F18.opExtrude","SWEPT_EDGE",EDGE,{"disambiguationData":[OSD([sQuery(id+"F17.wireOp",EDGE,"E48.8.0.0"),sQuery(id+"F17.wireOp",EDGE,"E48.8.0.1")])]});
            var Q21;
            Q21=makeQuery(id+"F18.opExtrude","SWEPT_EDGE",EDGE,{"disambiguationData":[OSD([sQuery(id+"F17.wireOp",EDGE,"E48.8.0.1"),sQuery(id+"F17.wireOp",EDGE,"E48.8.0.2")])]});
            var Q22;
            Q22=makeQuery(id+"F18.opExtrude","SWEPT_EDGE",EDGE,{"disambiguationData":[OSD([sQuery(id+"F17.wireOp",EDGE,"E48.9.0.0"),sQuery(id+"F17.wireOp",EDGE,"E48.9.0.1")])]});
            var Q23;
            Q23=makeQuery(id+"F18.opExtrude","SWEPT_EDGE",EDGE,{"disambiguationData":[OSD([sQuery(id+"F17.wireOp",EDGE,"E48.9.0.1"),sQuery(id+"F17.wireOp",EDGE,"E48.9.0.2")])]});
            var Q24;
            Q24=makeQuery(id+"F18.opExtrude","SWEPT_EDGE",EDGE,{"disambiguationData":[OSD([sQuery(id+"F17.wireOp",EDGE,"E48.10.0.0"),sQuery(id+"F17.wireOp",EDGE,"E48.10.0.1")])]});
            var Q25;
            Q25=makeQuery(id+"F18.opExtrude","SWEPT_EDGE",EDGE,{"disambiguationData":[OSD([sQuery(id+"F17.wireOp",EDGE,"E48.10.0.1"),sQuery(id+"F17.wireOp",EDGE,"E48.10.0.2")])]});
            var Q26;
            Q26=makeQuery(id+"F18.opExtrude","SWEPT_EDGE",EDGE,{"disambiguationData":[OSD([sQuery(id+"F17.wireOp",EDGE,"E48.11.0.0"),sQuery(id+"F17.wireOp",EDGE,"E48.11.0.1")])]});
            var Q27;
            Q27=makeQuery(id+"F18.opExtrude","SWEPT_EDGE",EDGE,{"disambiguationData":[OSD([sQuery(id+"F17.wireOp",EDGE,"E48.11.0.1"),sQuery(id+"F17.wireOp",EDGE,"E48.11.0.2")])]});
            var Q28;
            Q28=makeQuery(id+"F18.opExtrude","SWEPT_EDGE",EDGE,{"disambiguationData":[OSD([sQuery(id+"F17.wireOp",EDGE,"E48.13.0.0"),sQuery(id+"F17.wireOp",EDGE,"E48.13.0.3")])]});
            var Q29;
            Q29=makeQuery(id+"F18.opExtrude","SWEPT_EDGE",EDGE,{"disambiguationData":[OSD([sQuery(id+"F17.wireOp",EDGE,"E48.13.0.2"),sQuery(id+"F17.wireOp",EDGE,"E48.13.0.3")])]});
            var Q30;
            Q30=makeQuery(id+"F18.opExtrude","SWEPT_EDGE",EDGE,{"disambiguationData":[OSD([sQuery(id+"F17.wireOp",EDGE,"E48.12.0.2"),sQuery(id+"F17.wireOp",EDGE,"E48.12.0.3")])]});
            var Q31;
            Q31=makeQuery(id+"F18.opExtrude","SWEPT_EDGE",EDGE,{"disambiguationData":[OSD([sQuery(id+"F17.wireOp",EDGE,"E48.12.0.0"),sQuery(id+"F17.wireOp",EDGE,"E48.12.0.3")])]});
            var Q32;
            Q32=makeQuery(id+"F18.opExtrude","SWEPT_EDGE",EDGE,{"disambiguationData":[OSD([sQuery(id+"F17.wireOp",EDGE,"E47.top"),sQuery(id+"F17.wireOp",EDGE,"E47.left")])]});
            var Q33;
            Q33=makeQuery(id+"F18.opExtrude","SWEPT_EDGE",EDGE,{"disambiguationData":[OSD([sQuery(id+"F17.wireOp",EDGE,"E47.top"),sQuery(id+"F17.wireOp",EDGE,"E47.right")])]});
            var Q34;
            Q34=makeQuery(id+"F18.opExtrude","SWEPT_EDGE",EDGE,{"disambiguationData":[OSD([sQuery(id+"F17.wireOp",EDGE,"E48.1.0.2"),sQuery(id+"F17.wireOp",EDGE,"E48.1.0.3")])]});
            var Q35;
            Q35=makeQuery(id+"F18.opExtrude","SWEPT_EDGE",EDGE,{"disambiguationData":[OSD([sQuery(id+"F17.wireOp",EDGE,"E48.1.0.0"),sQuery(id+"F17.wireOp",EDGE,"E48.1.0.3")])]});
            var Q36;
            Q36=makeQuery(id+"F18.opExtrude","SWEPT_EDGE",EDGE,{"disambiguationData":[OSD([sQuery(id+"F17.wireOp",EDGE,"E48.2.0.0"),sQuery(id+"F17.wireOp",EDGE,"E48.2.0.3")])]});
            var Q37;
            Q37=makeQuery(id+"F18.opExtrude","SWEPT_EDGE",EDGE,{"disambiguationData":[OSD([sQuery(id+"F17.wireOp",EDGE,"E48.2.0.2"),sQuery(id+"F17.wireOp",EDGE,"E48.2.0.3")])]});
            var Q38;
            Q38=makeQuery(id+"F18.opExtrude","SWEPT_EDGE",EDGE,{"disambiguationData":[OSD([sQuery(id+"F17.wireOp",EDGE,"E48.3.0.0"),sQuery(id+"F17.wireOp",EDGE,"E48.3.0.3")])]});
            var Q39;
            Q39=makeQuery(id+"F18.opExtrude","SWEPT_EDGE",EDGE,{"disambiguationData":[OSD([sQuery(id+"F17.wireOp",EDGE,"E48.3.0.2"),sQuery(id+"F17.wireOp",EDGE,"E48.3.0.3")])]});
            var Q40;
            Q40=makeQuery(id+"F18.opExtrude","SWEPT_EDGE",EDGE,{"disambiguationData":[OSD([sQuery(id+"F17.wireOp",EDGE,"E48.4.0.2"),sQuery(id+"F17.wireOp",EDGE,"E48.4.0.3")])]});
            var Q41;
            Q41=makeQuery(id+"F18.opExtrude","SWEPT_EDGE",EDGE,{"disambiguationData":[OSD([sQuery(id+"F17.wireOp",EDGE,"E48.4.0.0"),sQuery(id+"F17.wireOp",EDGE,"E48.4.0.3")])]});
            var Q42;
            Q42=makeQuery(id+"F18.opExtrude","SWEPT_EDGE",EDGE,{"disambiguationData":[OSD([sQuery(id+"F17.wireOp",EDGE,"E48.5.0.2"),sQuery(id+"F17.wireOp",EDGE,"E48.5.0.3")])]});
            var Q43;
            Q43=makeQuery(id+"F18.opExtrude","SWEPT_EDGE",EDGE,{"disambiguationData":[OSD([sQuery(id+"F17.wireOp",EDGE,"E48.5.0.0"),sQuery(id+"F17.wireOp",EDGE,"E48.5.0.3")])]});
            var Q44;
            Q44=makeQuery(id+"F18.opExtrude","SWEPT_EDGE",EDGE,{"disambiguationData":[OSD([sQuery(id+"F17.wireOp",EDGE,"E48.6.0.0"),sQuery(id+"F17.wireOp",EDGE,"E48.6.0.3")])]});
            var Q45;
            Q45=makeQuery(id+"F18.opExtrude","SWEPT_EDGE",EDGE,{"disambiguationData":[OSD([sQuery(id+"F17.wireOp",EDGE,"E48.6.0.2"),sQuery(id+"F17.wireOp",EDGE,"E48.6.0.3")])]});
            var Q46;
            Q46=makeQuery(id+"F18.opExtrude","SWEPT_EDGE",EDGE,{"disambiguationData":[OSD([sQuery(id+"F17.wireOp",EDGE,"E48.7.0.0"),sQuery(id+"F17.wireOp",EDGE,"E48.7.0.3")])]});
            var Q47;
            Q47=makeQuery(id+"F18.opExtrude","SWEPT_EDGE",EDGE,{"disambiguationData":[OSD([sQuery(id+"F17.wireOp",EDGE,"E48.7.0.2"),sQuery(id+"F17.wireOp",EDGE,"E48.7.0.3")])]});
            var Q48;
            Q48=makeQuery(id+"F18.opExtrude","SWEPT_EDGE",EDGE,{"disambiguationData":[OSD([sQuery(id+"F17.wireOp",EDGE,"E48.8.0.2"),sQuery(id+"F17.wireOp",EDGE,"E48.8.0.3")])]});
            var Q49;
            Q49=makeQuery(id+"F18.opExtrude","SWEPT_EDGE",EDGE,{"disambiguationData":[OSD([sQuery(id+"F17.wireOp",EDGE,"E48.8.0.0"),sQuery(id+"F17.wireOp",EDGE,"E48.8.0.3")])]});
            var Q50;
            Q50=makeQuery(id+"F18.opExtrude","SWEPT_EDGE",EDGE,{"disambiguationData":[OSD([sQuery(id+"F17.wireOp",EDGE,"E48.9.0.0"),sQuery(id+"F17.wireOp",EDGE,"E48.9.0.3")])]});
            var Q51;
            Q51=makeQuery(id+"F18.opExtrude","SWEPT_EDGE",EDGE,{"disambiguationData":[OSD([sQuery(id+"F17.wireOp",EDGE,"E48.9.0.2"),sQuery(id+"F17.wireOp",EDGE,"E48.9.0.3")])]});
            var Q52;
            Q52=makeQuery(id+"F18.opExtrude","SWEPT_EDGE",EDGE,{"disambiguationData":[OSD([sQuery(id+"F17.wireOp",EDGE,"E48.10.0.0"),sQuery(id+"F17.wireOp",EDGE,"E48.10.0.3")])]});
            var Q53;
            Q53=makeQuery(id+"F18.opExtrude","SWEPT_EDGE",EDGE,{"disambiguationData":[OSD([sQuery(id+"F17.wireOp",EDGE,"E48.10.0.2"),sQuery(id+"F17.wireOp",EDGE,"E48.10.0.3")])]});
            var Q54;
            Q54=makeQuery(id+"F18.opExtrude","SWEPT_EDGE",EDGE,{"disambiguationData":[OSD([sQuery(id+"F17.wireOp",EDGE,"E48.11.0.2"),sQuery(id+"F17.wireOp",EDGE,"E48.11.0.3")])]});
            var Q55;
            Q55=makeQuery(id+"F18.opExtrude","SWEPT_EDGE",EDGE,{"disambiguationData":[OSD([sQuery(id+"F17.wireOp",EDGE,"E48.11.0.0"),sQuery(id+"F17.wireOp",EDGE,"E48.11.0.3")])]});
            fillet(context, id + "F21", {"entities" : qUnion([Q0, Q1, Q2, Q3, Q4, Q5, Q6, Q7, Q8, Q9, Q10, Q11, Q12, Q13, Q14, Q15, Q16, Q17, Q18, Q19, Q20, Q21, Q22, Q23, Q24, Q25, Q26, Q27, Q28, Q29, Q30, Q31, Q32, Q33, Q34, Q35, Q36, Q37, Q38, Q39, Q40, Q41, Q42, Q43, Q44, Q45, Q46, Q47, Q48, Q49, Q50, Q51, Q52, Q53, Q54, Q55]), "radius" : 2 * mm, "tangentPropagation" : true, "allowEdgeOverflow" : false});
        }
        {
            var Q0;
            Q0=makeQuery(id+"F15.opExtrude","SWEPT_FACE",FACE,{"disambiguationData":[OSD([sQuery(id+"F14.wireOp",EDGE,"E37.left"),sQuery(id+"F14.wireOp",EDGE,"E38.right")])]});
            var sketch = newSketch(context, id + "F22", { "sketchPlane" : qUnion([Q0])});
            skLineSegment(sketch, "E49.bottom", {"start": v(42, 784) * mm, "end": v(1774, 784) * mm});
            skLineSegment(sketch, "E49.top", {"start": v(42, 934) * mm, "end": v(1774, 934) * mm});
            skLineSegment(sketch, "E49.left", {"start": v(42, 784) * mm, "end": v(42, 934) * mm});
            skLineSegment(sketch, "E49.right", {"start": v(1774, 784) * mm, "end": v(1774, 934) * mm});
            skSolve(sketch);
        }
        {
            var Q0;
            Q0 = qSketchRegion(id + "F22", true);
            var Q1;
            Q1=makeQuery(id+"F2.opExtrude","CAP_FACE",FACE,{"disambiguationData":[OSD([sQuery(id+"F0.wireOp",EDGE,"E1.bottom"),sQuery(id+"F0.wireOp",EDGE,"E1.top"),sQuery(id+"F0.wireOp",EDGE,"E1.left"),sQuery(id+"F0.wireOp",EDGE,"E2.left")])],"isStart":true});
            extrude(context, id + "F23", {"entities" : qUnion([Q0]), "endBound" : BoundingType.UP_TO_SURFACE, "endBoundEntityFace" : qUnion([Q1]), "depth" : 25 * mm});
        }
        {
            var Q0;
            Q0=makeQuery(id+"F23.opExtrude","SWEPT_EDGE",EDGE,{"disambiguationData":[OSD([sQuery(id+"F22.wireOp",EDGE,"E49.bottom"),sQuery(id+"F22.wireOp",EDGE,"E49.left")])]});
            var Q1;
            Q1=makeQuery(id+"F23.opExtrude","SWEPT_EDGE",EDGE,{"disambiguationData":[OSD([sQuery(id+"F22.wireOp",EDGE,"E49.top"),sQuery(id+"F22.wireOp",EDGE,"E49.right")])]});
            var Q2;
            Q2=makeQuery(id+"F23.opExtrude","TWEAK_EDGE",EDGE,{"derivedFrom":[makeQuery(id+"F2.opExtrude","CAP_FACE",FACE,{"disambiguationData":[OSD([sQuery(id+"F0.wireOp",EDGE,"E1.bottom"),sQuery(id+"F0.wireOp",EDGE,"E1.top"),sQuery(id+"F0.wireOp",EDGE,"E1.left"),sQuery(id+"F0.wireOp",EDGE,"E2.left")])],"isStart":true}),makeQuery(id+"F22.imprint","IMPRINT",EDGE,{"derivedFrom":sQuery(id+"F22.wireOp",EDGE,"E49.top")})]});
            var Q3;
            Q3=makeQuery(id+"F23.opExtrude","CAP_EDGE",EDGE,{"disambiguationData":[OSD([sQuery(id+"F22.wireOp",EDGE,"E49.left")])],"isStart":true});
            var Q4;
            Q4=makeQuery(id+"F23.opExtrude","CAP_EDGE",EDGE,{"disambiguationData":[OSD([sQuery(id+"F22.wireOp",EDGE,"E49.top")])],"isStart":true});
            var Q5;
            Q5=makeQuery(id+"F23.opExtrude","CAP_EDGE",EDGE,{"disambiguationData":[OSD([sQuery(id+"F22.wireOp",EDGE,"E49.bottom")])],"isStart":true});
            var Q6;
            Q6=makeQuery(id+"F23.opExtrude","SWEPT_EDGE",EDGE,{"disambiguationData":[OSD([sQuery(id+"F22.wireOp",EDGE,"E49.top"),sQuery(id+"F22.wireOp",EDGE,"E49.left")])]});
            var Q7;
            Q7=makeQuery(id+"F23.opExtrude","TWEAK_EDGE",EDGE,{"derivedFrom":[makeQuery(id+"F2.opExtrude","CAP_FACE",FACE,{"disambiguationData":[OSD([sQuery(id+"F0.wireOp",EDGE,"E1.bottom"),sQuery(id+"F0.wireOp",EDGE,"E1.top"),sQuery(id+"F0.wireOp",EDGE,"E1.left"),sQuery(id+"F0.wireOp",EDGE,"E2.left")])],"isStart":true}),makeQuery(id+"F22.imprint","IMPRINT",EDGE,{"derivedFrom":sQuery(id+"F22.wireOp",EDGE,"E49.left")})]});
            var Q8;
            {var subQ0=sQuery(id+"F22.wireOp",EDGE,"E49.bottom");var subQ1=sQuery(id+"F14.wireOp",EDGE,"E38.right");var subQ2=sQuery(id+"F14.wireOp",EDGE,"E37.left");var subQ3=makeQuery(id+"F15.opExtrude","SWEPT_FACE",FACE,{"disambiguationData":[OSD([subQ2,subQ1])]});var subQ5=makeQuery(id+"F22.imprint","INTERSECT",VERTEX,{"derivedFrom":[makeQuery(id+"F44feBJewh3kdJR_33.opFillet","BLEND_EDGE",EDGE,{"blendedFrom":[makeQuery(id+"F15.opExtrude","CAP_EDGE",EDGE,{"disambiguationData":[OSD([subQ2,subQ1])],"isStart":true}),subQ3],"blendedInto":[subQ3]}),subQ0]});Q8=makeQuery(id+"F23.opExtrude","TWEAK_EDGE",EDGE,{"derivedFrom":[makeQuery(id+"F2.opExtrude","CAP_FACE",FACE,{"disambiguationData":[OSD([sQuery(id+"F0.wireOp",EDGE,"E1.bottom"),sQuery(id+"F0.wireOp",EDGE,"E1.top"),sQuery(id+"F0.wireOp",EDGE,"E1.left"),sQuery(id+"F0.wireOp",EDGE,"E2.left")])],"isStart":true}),makeQuery(id+"F22.imprint","IMPRINT",EDGE,{"disambiguationData":[TD([[makeQuery(id+"F22.imprint","INTERSECT",VERTEX,{"derivedFrom":[subQ0,sQuery(id+"F22.wireOp",EDGE,"E49.left")]}),-1.0]])],"derivedFrom":subQ0}),makeQuery(id+"F22.imprint","IMPRINT",EDGE,{"disambiguationData":[TD([[subQ5,-1.0]])],"derivedFrom":subQ0}),makeQuery(id+"F22.imprint","IMPRINT",EDGE,{"disambiguationData":[TD([[makeQuery(id+"F22.imprint","INTERSECT",VERTEX,{"derivedFrom":[subQ0,sQuery(id+"F22.wireOp",EDGE,"E49.right")]}),1.0]])],"derivedFrom":subQ0})]});}
            var Q9;
            Q9=makeQuery(id+"F23.opExtrude","TWEAK_EDGE",EDGE,{"derivedFrom":[makeQuery(id+"F2.opExtrude","CAP_FACE",FACE,{"disambiguationData":[OSD([sQuery(id+"F0.wireOp",EDGE,"E1.bottom"),sQuery(id+"F0.wireOp",EDGE,"E1.top"),sQuery(id+"F0.wireOp",EDGE,"E1.left"),sQuery(id+"F0.wireOp",EDGE,"E2.left")])],"isStart":true}),makeQuery(id+"F22.imprint","IMPRINT",EDGE,{"derivedFrom":sQuery(id+"F22.wireOp",EDGE,"E49.right")})]});
            var Q10;
            Q10=makeQuery(id+"F23.opExtrude","SWEPT_EDGE",EDGE,{"disambiguationData":[OSD([sQuery(id+"F22.wireOp",EDGE,"E49.bottom"),sQuery(id+"F22.wireOp",EDGE,"E49.right")])]});
            var Q11;
            Q11=makeQuery(id+"F23.opExtrude","CAP_EDGE",EDGE,{"disambiguationData":[OSD([sQuery(id+"F22.wireOp",EDGE,"E49.right")])],"isStart":true});
            fillet(context, id + "F24", {"entities" : qUnion([Q0, Q1, Q2, Q3, Q4, Q5, Q6, Q7, Q8, Q9, Q10, Q11]), "radius" : 15 * mm, "tangentPropagation" : true, "allowEdgeOverflow" : false});
        }
    });
